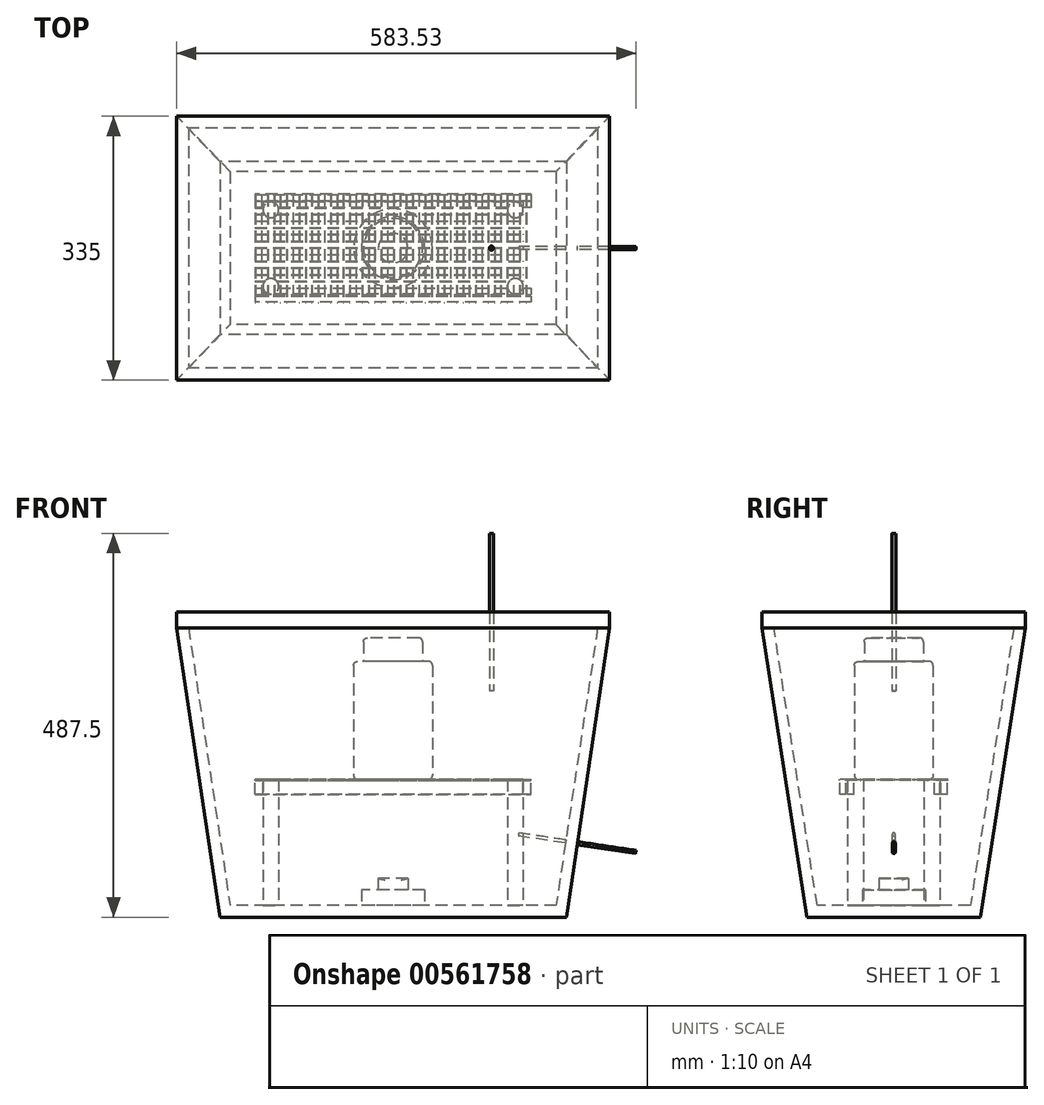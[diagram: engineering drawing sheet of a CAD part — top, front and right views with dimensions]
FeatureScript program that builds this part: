
annotation { "Feature Type Name" : "Feature", "Feature Type Description" : "" }
export const myFeature = defineFeature(function(context is Context, id is Id, definition is map)
    precondition{}
    {
        {
            var Q0;
            Q0=qCreatedBy(makeId("Top.planeOp"),FACE);
            cPlane(context, id + "F0", {"entities" : qUnion([Q0]), "cplaneType" : CPlaneType.OFFSET, "offset" : 200 * mm, "width" : 150 * mm, "height" : 150 * mm});
        }
        {
            var Q0;
            Q0=qCreatedBy(makeId("Top.planeOp"),FACE);
            cPlane(context, id + "F1", {"entities" : qUnion([Q0]), "cplaneType" : CPlaneType.OFFSET, "offset" : 167.5 * mm, "oppositeDirection" : true, "width" : 150 * mm, "height" : 150 * mm});
        }
        {
            var Q0;
            Q0=qCreatedBy(id+"F1.planeOp",FACE);
            var sketch = newSketch(context, id + "F2", { "sketchPlane" : qUnion([Q0])});
            skLineSegment(sketch, "E0.bottom", {"start": v(220, 110) * mm, "end": v(-220, 110) * mm});
            skLineSegment(sketch, "E0.top", {"start": v(220, -110) * mm, "end": v(-220, -110) * mm});
            skLineSegment(sketch, "E0.left", {"start": v(220, 110) * mm, "end": v(220, -110) * mm});
            skLineSegment(sketch, "E0.right", {"start": v(-220, 110) * mm, "end": v(-220, -110) * mm});
            skPoint(sketch, "E0.middle", {"position": v(0, 0) * mm});
            skSolve(sketch);
        }
        {
            var Q0;
            Q0=qCreatedBy(id+"F0.planeOp",FACE);
            var sketch = newSketch(context, id + "F3", { "sketchPlane" : qUnion([Q0])});
            skLineSegment(sketch, "E1.bottom", {"start": v(275, 167.5) * mm, "end": v(-275, 167.5) * mm});
            skLineSegment(sketch, "E1.top", {"start": v(275, -167.5) * mm, "end": v(-275, -167.5) * mm});
            skLineSegment(sketch, "E1.left", {"start": v(275, 167.5) * mm, "end": v(275, -167.5) * mm});
            skLineSegment(sketch, "E1.right", {"start": v(-275, 167.5) * mm, "end": v(-275, -167.5) * mm});
            skPoint(sketch, "E1.middle", {"position": v(0, 0) * mm});
            skSolve(sketch);
        }
        {
            var Q0;
            Q0=makeQuery(id+"F2.imprint","IMPRINT",FACE,{"disambiguationData":[TD([[makeQuery(id+"F2.imprint","IMPRINT",EDGE,{"derivedFrom":sQuery(id+"F2.wireOp",EDGE,"E0.bottom")}),1.0]])]});
            var Q1;
            Q1=makeQuery(id+"F3.imprint","IMPRINT",FACE,{"disambiguationData":[TD([[makeQuery(id+"F3.imprint","IMPRINT",EDGE,{"derivedFrom":sQuery(id+"F3.wireOp",EDGE,"E1.bottom")}),1.0]])]});
            loft(context, id + "F4", {"sheetProfilesArray" : [{ "sheetProfileEntities" : qUnion([Q0]) }, { "sheetProfileEntities" : qUnion([Q1]) }]});
        }
        {
            var Q0;
            Q0=makeQuery(id+"F4.opLoft","CAP_FACE",FACE,{"disambiguationData":[OSD([makeQuery(id+"F3.imprint","IMPRINT",FACE,{"disambiguationData":[TD([[makeQuery(id+"F3.imprint","IMPRINT",EDGE,{"derivedFrom":sQuery(id+"F3.wireOp",EDGE,"E1.bottom")}),1.0]])]})])],"isStart":true});
            shell(context, id + "F5", {"entities" : qUnion([Q0]), "thickness" : 15 * mm});
        }
        {
            var Q0;
            Q0=makeQuery(id+"F5.opShell","OFFSET_FACE",FACE,{"disambiguationData":[OSD([makeQuery(id+"F2.imprint","IMPRINT",FACE,{"disambiguationData":[TD([[makeQuery(id+"F2.imprint","IMPRINT",EDGE,{"derivedFrom":sQuery(id+"F2.wireOp",EDGE,"E0.bottom")}),1.0]])]})])]});
            var sketch = newSketch(context, id + "F6", { "sketchPlane" : qUnion([Q0])});
            skCircle(sketch, "E2", {"center": v(-155.28, 48.56) * mm, "radius": 10 * mm});
            skCircle(sketch, "E3", {"center": v(-155.28, -48.56) * mm, "radius": 10 * mm});
            skCircle(sketch, "E4", {"center": v(155.28, -48.56) * mm, "radius": 10 * mm});
            skCircle(sketch, "E5", {"center": v(155.28, 48.56) * mm, "radius": 10 * mm});
            skSolve(sketch);
        }
        {
            var Q0;
            Q0=makeQuery(id+"F6.imprint","IMPRINT",FACE,{"disambiguationData":[TD([[makeQuery(id+"F6.imprint","IMPRINT",EDGE,{"derivedFrom":sQuery(id+"F6.wireOp",EDGE,"E2")}),1.0]])]});
            var Q1;
            Q1=makeQuery(id+"F6.imprint","IMPRINT",FACE,{"disambiguationData":[TD([[makeQuery(id+"F6.imprint","IMPRINT",EDGE,{"derivedFrom":sQuery(id+"F6.wireOp",EDGE,"E3")}),1.0]])]});
            var Q2;
            Q2=makeQuery(id+"F6.imprint","IMPRINT",FACE,{"disambiguationData":[TD([[makeQuery(id+"F6.imprint","IMPRINT",EDGE,{"derivedFrom":sQuery(id+"F6.wireOp",EDGE,"E5")}),1.0]])]});
            var Q3;
            Q3=makeQuery(id+"F6.imprint","IMPRINT",FACE,{"disambiguationData":[TD([[makeQuery(id+"F6.imprint","IMPRINT",EDGE,{"derivedFrom":sQuery(id+"F6.wireOp",EDGE,"E4")}),1.0]])]});
            extrude(context, id + "F7", {"entities" : qUnion([Q0, Q1, Q2, Q3]), "operationType" : NewBodyOperationType.ADD, "depth" : 160 * mm, "offsetDistance" : 25 * mm});
        }
        {
            var Q0;
            Q0=makeQuery(id+"F7.opExtrude","CAP_FACE",FACE,{"disambiguationData":[OSD([sQuery(id+"F6.wireOp",EDGE,"E2")])],"isStart":false});
            var sketch = newSketch(context, id + "F8", { "sketchPlane" : qUnion([Q0])});
            skLineSegment(sketch, "E6.bottom", {"start": v(-155.28, 48.56) * mm, "end": v(155.28, 48.56) * mm});
            skLineSegment(sketch, "E6.top", {"start": v(-155.28, -48.56) * mm, "end": v(155.28, -48.56) * mm});
            skLineSegment(sketch, "E6.left", {"start": v(-155.28, 48.56) * mm, "end": v(-155.28, -48.56) * mm});
            skLineSegment(sketch, "E6.right", {"start": v(155.28, 48.56) * mm, "end": v(155.28, -48.56) * mm});
            skPoint(sketch, "E6.middle", {"position": v(0, 0) * mm});
            skLineSegment(sketch, "E7.bottom", {"start": v(165.28, 58.56) * mm, "end": v(-165.28, 58.56) * mm});
            skLineSegment(sketch, "E7.top", {"start": v(165.28, -58.56) * mm, "end": v(-165.28, -58.56) * mm});
            skLineSegment(sketch, "E7.left", {"start": v(165.28, 58.56) * mm, "end": v(165.28, -58.56) * mm});
            skLineSegment(sketch, "E7.right", {"start": v(-165.28, 58.56) * mm, "end": v(-165.28, -58.56) * mm});
            skLineSegment(sketch, "E8.bottom", {"start": v(175.28, 68.56) * mm, "end": v(-175.28, 68.56) * mm});
            skLineSegment(sketch, "E8.top", {"start": v(175.28, -68.56) * mm, "end": v(-175.28, -68.56) * mm});
            skLineSegment(sketch, "E8.left", {"start": v(175.28, 68.56) * mm, "end": v(175.28, -68.56) * mm});
            skLineSegment(sketch, "E8.right", {"start": v(-175.28, 68.56) * mm, "end": v(-175.28, -68.56) * mm});
            skLineSegment(sketch, "E9.bottom", {"start": v(-175.28, 68.06) * mm, "end": v(175.28, 68.06) * mm});
            skLineSegment(sketch, "E9.top", {"start": v(-175.28, 60.06) * mm, "end": v(175.28, 60.06) * mm});
            skLineSegment(sketch, "E9.left", {"start": v(-175.28, 68.06) * mm, "end": v(-175.28, 60.06) * mm});
            skLineSegment(sketch, "E9.right", {"start": v(175.28, 68.06) * mm, "end": v(175.28, 60.06) * mm});
            skLineSegment(sketch, "E10.bottom", {"start": v(175.28, 59.56) * mm, "end": v(-175.28, 59.56) * mm});
            skLineSegment(sketch, "E10.top", {"start": v(175.28, 51.56) * mm, "end": v(-175.28, 51.56) * mm});
            skLineSegment(sketch, "E10.left", {"start": v(175.28, 59.56) * mm, "end": v(175.28, 51.56) * mm});
            skLineSegment(sketch, "E10.right", {"start": v(-175.28, 59.56) * mm, "end": v(-175.28, 51.56) * mm});
            skLineSegment(sketch, "E11.bottom", {"start": v(-175.28, 43.06) * mm, "end": v(175.28, 43.06) * mm});
            skLineSegment(sketch, "E11.top", {"start": v(-175.28, 51.06) * mm, "end": v(175.28, 51.06) * mm});
            skLineSegment(sketch, "E11.left", {"start": v(-175.28, 43.06) * mm, "end": v(-175.28, 51.06) * mm});
            skLineSegment(sketch, "E11.right", {"start": v(175.28, 43.06) * mm, "end": v(175.28, 51.06) * mm});
            skLineSegment(sketch, "E12.bottom", {"start": v(-175.28, 42.56) * mm, "end": v(175.28, 42.56) * mm});
            skLineSegment(sketch, "E12.top", {"start": v(-175.28, 34.56) * mm, "end": v(175.28, 34.56) * mm});
            skLineSegment(sketch, "E12.left", {"start": v(-175.28, 42.56) * mm, "end": v(-175.28, 34.56) * mm});
            skLineSegment(sketch, "E12.right", {"start": v(175.28, 42.56) * mm, "end": v(175.28, 34.56) * mm});
            skLineSegment(sketch, "E13.bottom", {"start": v(-175.28, 34.06) * mm, "end": v(175.28, 34.06) * mm});
            skLineSegment(sketch, "E13.top", {"start": v(-175.28, 26.06) * mm, "end": v(175.28, 26.06) * mm});
            skLineSegment(sketch, "E13.left", {"start": v(-175.28, 34.06) * mm, "end": v(-175.28, 26.06) * mm});
            skLineSegment(sketch, "E13.right", {"start": v(175.28, 34.06) * mm, "end": v(175.28, 26.06) * mm});
            skLineSegment(sketch, "E14.bottom", {"start": v(-175.28, 25.56) * mm, "end": v(175.28, 25.56) * mm});
            skLineSegment(sketch, "E14.top", {"start": v(-175.28, 17.56) * mm, "end": v(175.28, 17.56) * mm});
            skLineSegment(sketch, "E14.left", {"start": v(-175.28, 25.56) * mm, "end": v(-175.28, 17.56) * mm});
            skLineSegment(sketch, "E14.right", {"start": v(175.28, 25.56) * mm, "end": v(175.28, 17.56) * mm});
            skLineSegment(sketch, "E15.bottom", {"start": v(-175.28, 17.06) * mm, "end": v(175.28, 17.06) * mm});
            skLineSegment(sketch, "E15.top", {"start": v(-175.28, 9.06) * mm, "end": v(175.28, 9.06) * mm});
            skLineSegment(sketch, "E15.left", {"start": v(-175.28, 17.06) * mm, "end": v(-175.28, 9.06) * mm});
            skLineSegment(sketch, "E15.right", {"start": v(175.28, 17.06) * mm, "end": v(175.28, 9.06) * mm});
            skLineSegment(sketch, "E16.bottom", {"start": v(-175.28, 0.56) * mm, "end": v(175.28, 0.56) * mm});
            skLineSegment(sketch, "E16.top", {"start": v(-175.28, 8.56) * mm, "end": v(175.28, 8.56) * mm});
            skLineSegment(sketch, "E16.left", {"start": v(-175.28, 0.56) * mm, "end": v(-175.28, 8.56) * mm});
            skLineSegment(sketch, "E16.right", {"start": v(175.28, 0.56) * mm, "end": v(175.28, 8.56) * mm});
            skLineSegment(sketch, "E17.bottom", {"start": v(-175.28, -7.94) * mm, "end": v(175.28, -7.94) * mm});
            skLineSegment(sketch, "E17.top", {"start": v(-175.28, 0.06) * mm, "end": v(175.28, 0.06) * mm});
            skLineSegment(sketch, "E17.left", {"start": v(-175.28, -7.94) * mm, "end": v(-175.28, 0.06) * mm});
            skLineSegment(sketch, "E17.right", {"start": v(175.28, -7.94) * mm, "end": v(175.28, 0.06) * mm});
            skLineSegment(sketch, "E18.bottom", {"start": v(-175.28, -8.44) * mm, "end": v(175.28, -8.44) * mm});
            skLineSegment(sketch, "E18.top", {"start": v(-175.28, -16.44) * mm, "end": v(175.28, -16.44) * mm});
            skLineSegment(sketch, "E18.left", {"start": v(-175.28, -8.44) * mm, "end": v(-175.28, -16.44) * mm});
            skLineSegment(sketch, "E18.right", {"start": v(175.28, -8.44) * mm, "end": v(175.28, -16.44) * mm});
            skLineSegment(sketch, "E19.bottom", {"start": v(-175.28, -16.94) * mm, "end": v(175.28, -16.94) * mm});
            skLineSegment(sketch, "E19.top", {"start": v(-175.28, -24.94) * mm, "end": v(175.28, -24.94) * mm});
            skLineSegment(sketch, "E19.left", {"start": v(-175.28, -16.94) * mm, "end": v(-175.28, -24.94) * mm});
            skLineSegment(sketch, "E19.right", {"start": v(175.28, -16.94) * mm, "end": v(175.28, -24.94) * mm});
            skLineSegment(sketch, "E20.bottom", {"start": v(-175.28, -25.44) * mm, "end": v(175.28, -25.44) * mm});
            skLineSegment(sketch, "E20.top", {"start": v(-175.28, -33.44) * mm, "end": v(175.28, -33.44) * mm});
            skLineSegment(sketch, "E20.left", {"start": v(-175.28, -25.44) * mm, "end": v(-175.28, -33.44) * mm});
            skLineSegment(sketch, "E20.right", {"start": v(175.28, -25.44) * mm, "end": v(175.28, -33.44) * mm});
            skLineSegment(sketch, "E21.bottom", {"start": v(-175.28, -33.94) * mm, "end": v(175.28, -33.94) * mm});
            skLineSegment(sketch, "E21.top", {"start": v(-175.28, -41.94) * mm, "end": v(175.28, -41.94) * mm});
            skLineSegment(sketch, "E21.left", {"start": v(-175.28, -33.94) * mm, "end": v(-175.28, -41.94) * mm});
            skLineSegment(sketch, "E21.right", {"start": v(175.28, -33.94) * mm, "end": v(175.28, -41.94) * mm});
            skLineSegment(sketch, "E22.bottom", {"start": v(-175.28, -42.44) * mm, "end": v(175.28, -42.44) * mm});
            skLineSegment(sketch, "E22.top", {"start": v(-175.28, -50.44) * mm, "end": v(175.28, -50.44) * mm});
            skLineSegment(sketch, "E22.left", {"start": v(-175.28, -42.44) * mm, "end": v(-175.28, -50.44) * mm});
            skLineSegment(sketch, "E22.right", {"start": v(175.28, -42.44) * mm, "end": v(175.28, -50.44) * mm});
            skLineSegment(sketch, "E23.bottom", {"start": v(-175.28, -50.94) * mm, "end": v(175.28, -50.94) * mm});
            skLineSegment(sketch, "E23.top", {"start": v(-175.28, -58.94) * mm, "end": v(175.28, -58.94) * mm});
            skLineSegment(sketch, "E23.left", {"start": v(-175.28, -50.94) * mm, "end": v(-175.28, -58.94) * mm});
            skLineSegment(sketch, "E23.right", {"start": v(175.28, -50.94) * mm, "end": v(175.28, -58.94) * mm});
            skLineSegment(sketch, "E24.bottom", {"start": v(-175.28, -60.56) * mm, "end": v(175.28, -60.56) * mm});
            skLineSegment(sketch, "E24.top", {"start": v(-175.28, -68.56) * mm, "end": v(175.28, -68.56) * mm});
            skLineSegment(sketch, "E24.left", {"start": v(-175.28, -60.56) * mm, "end": v(-175.28, -68.56) * mm});
            skLineSegment(sketch, "E24.right", {"start": v(175.28, -60.56) * mm, "end": v(175.28, -68.56) * mm});
            skSolve(sketch);
        }
        {
            var Q0;
            {var subQ5=sQuery(id+"F8.wireOp",EDGE,"E7.top");Q0=makeQuery(id+"F8.imprint","IMPRINT",FACE,{"disambiguationData":[TD([[makeQuery(id+"F8.imprint","IMPRINT",EDGE,{"derivedFrom":subQ5}),1.0]])]});}
            var Q1;
            {var subQ0=sQuery(id+"F8.wireOp",EDGE,"E16.bottom");var subQ1=sQuery(id+"F8.wireOp",EDGE,"E7.right");var subQ2=makeQuery(id+"F8.imprint","INTERSECT",VERTEX,{"derivedFrom":[subQ1,subQ0]});Q1=makeQuery(id+"F8.imprint","IMPRINT",FACE,{"disambiguationData":[TD([[makeQuery(id+"F8.imprint","IMPRINT",EDGE,{"disambiguationData":[TD([[subQ2,-1.0]])],"derivedFrom":subQ1}),-1.0]])]});}
            var Q2;
            {var subQ0=sQuery(id+"F8.wireOp",EDGE,"E13.top");var subQ1=sQuery(id+"F8.wireOp",EDGE,"E7.right");var subQ2=makeQuery(id+"F8.imprint","INTERSECT",VERTEX,{"derivedFrom":[subQ1,subQ0]});Q2=makeQuery(id+"F8.imprint","IMPRINT",FACE,{"disambiguationData":[TD([[makeQuery(id+"F8.imprint","IMPRINT",EDGE,{"disambiguationData":[TD([[subQ2,-1.0]])],"derivedFrom":subQ1}),-1.0]])]});}
            var Q3;
            {var subQ0=sQuery(id+"F8.wireOp",EDGE,"E13.top");var subQ1=sQuery(id+"F8.wireOp",EDGE,"E6.right");var subQ2=makeQuery(id+"F8.imprint","INTERSECT",VERTEX,{"derivedFrom":[subQ1,subQ0]});Q3=makeQuery(id+"F8.imprint","IMPRINT",FACE,{"disambiguationData":[TD([[makeQuery(id+"F8.imprint","IMPRINT",EDGE,{"disambiguationData":[TD([[subQ2,-1.0]])],"derivedFrom":subQ1}),1.0]])]});}
            var Q4;
            {var subQ0=sQuery(id+"F8.wireOp",EDGE,"E13.top");var subQ1=sQuery(id+"F8.wireOp",EDGE,"E6.left");var subQ2=makeQuery(id+"F8.imprint","INTERSECT",VERTEX,{"derivedFrom":[subQ1,subQ0]});Q4=makeQuery(id+"F8.imprint","IMPRINT",FACE,{"disambiguationData":[TD([[makeQuery(id+"F8.imprint","IMPRINT",EDGE,{"disambiguationData":[TD([[subQ2,-1.0]])],"derivedFrom":subQ1}),-1.0]])]});}
            var Q5;
            {var subQ0=sQuery(id+"F8.wireOp",EDGE,"E20.top");var subQ1=sQuery(id+"F8.wireOp",EDGE,"E6.left");var subQ2=makeQuery(id+"F8.imprint","INTERSECT",VERTEX,{"derivedFrom":[subQ1,subQ0]});Q5=makeQuery(id+"F8.imprint","IMPRINT",FACE,{"disambiguationData":[TD([[makeQuery(id+"F8.imprint","IMPRINT",EDGE,{"disambiguationData":[TD([[subQ2,-1.0]])],"derivedFrom":subQ1}),-1.0]])]});}
            var Q6;
            {var subQ0=sQuery(id+"F8.wireOp",EDGE,"E16.bottom");var subQ1=sQuery(id+"F8.wireOp",EDGE,"E6.left");var subQ2=makeQuery(id+"F8.imprint","INTERSECT",VERTEX,{"derivedFrom":[subQ1,subQ0]});Q6=makeQuery(id+"F8.imprint","IMPRINT",FACE,{"disambiguationData":[TD([[makeQuery(id+"F8.imprint","IMPRINT",EDGE,{"disambiguationData":[TD([[subQ2,-1.0]])],"derivedFrom":subQ1}),-1.0]])]});}
            var Q7;
            {var subQ0=sQuery(id+"F8.wireOp",EDGE,"E15.top");var subQ1=sQuery(id+"F8.wireOp",EDGE,"E6.left");var subQ2=makeQuery(id+"F8.imprint","INTERSECT",VERTEX,{"derivedFrom":[subQ1,subQ0]});Q7=makeQuery(id+"F8.imprint","IMPRINT",FACE,{"disambiguationData":[TD([[makeQuery(id+"F8.imprint","IMPRINT",EDGE,{"disambiguationData":[TD([[subQ2,-1.0]])],"derivedFrom":subQ1}),1.0]])]});}
            var Q8;
            {var subQ0=sQuery(id+"F8.wireOp",EDGE,"E19.top");var subQ1=sQuery(id+"F8.wireOp",EDGE,"E6.left");var subQ2=makeQuery(id+"F8.imprint","INTERSECT",VERTEX,{"derivedFrom":[subQ1,subQ0]});Q8=makeQuery(id+"F8.imprint","IMPRINT",FACE,{"disambiguationData":[TD([[makeQuery(id+"F8.imprint","IMPRINT",EDGE,{"disambiguationData":[TD([[subQ2,-1.0]])],"derivedFrom":subQ1}),1.0]])]});}
            var Q9;
            {var subQ0=sQuery(id+"F8.wireOp",EDGE,"E12.top");var subQ1=sQuery(id+"F8.wireOp",EDGE,"E6.left");var subQ2=makeQuery(id+"F8.imprint","INTERSECT",VERTEX,{"derivedFrom":[subQ1,subQ0]});Q9=makeQuery(id+"F8.imprint","IMPRINT",FACE,{"disambiguationData":[TD([[makeQuery(id+"F8.imprint","IMPRINT",EDGE,{"disambiguationData":[TD([[subQ2,-1.0]])],"derivedFrom":subQ1}),-1.0]])]});}
            var Q10;
            {var subQ0=sQuery(id+"F8.wireOp",EDGE,"E10.top");var subQ1=sQuery(id+"F8.wireOp",EDGE,"E7.left");var subQ2=makeQuery(id+"F8.imprint","INTERSECT",VERTEX,{"derivedFrom":[subQ1,subQ0]});Q10=makeQuery(id+"F8.imprint","IMPRINT",FACE,{"disambiguationData":[TD([[makeQuery(id+"F8.imprint","IMPRINT",EDGE,{"disambiguationData":[TD([[subQ2,-1.0]])],"derivedFrom":subQ1}),-1.0]])]});}
            var Q11;
            {var subQ0=sQuery(id+"F8.wireOp",EDGE,"E16.bottom");var subQ1=sQuery(id+"F8.wireOp",EDGE,"E6.right");var subQ2=makeQuery(id+"F8.imprint","INTERSECT",VERTEX,{"derivedFrom":[subQ1,subQ0]});Q11=makeQuery(id+"F8.imprint","IMPRINT",FACE,{"disambiguationData":[TD([[makeQuery(id+"F8.imprint","IMPRINT",EDGE,{"disambiguationData":[TD([[subQ2,-1.0]])],"derivedFrom":subQ1}),1.0]])]});}
            var Q12;
            {var subQ0=sQuery(id+"F8.wireOp",EDGE,"E18.top");var subQ1=sQuery(id+"F8.wireOp",EDGE,"E6.left");var subQ2=makeQuery(id+"F8.imprint","INTERSECT",VERTEX,{"derivedFrom":[subQ1,subQ0]});Q12=makeQuery(id+"F8.imprint","IMPRINT",FACE,{"disambiguationData":[TD([[makeQuery(id+"F8.imprint","IMPRINT",EDGE,{"disambiguationData":[TD([[subQ2,-1.0]])],"derivedFrom":subQ1}),-1.0]])]});}
            var Q13;
            {var subQ0=sQuery(id+"F8.wireOp",EDGE,"E17.bottom");var subQ1=sQuery(id+"F8.wireOp",EDGE,"E6.right");var subQ2=makeQuery(id+"F8.imprint","INTERSECT",VERTEX,{"derivedFrom":[subQ1,subQ0]});Q13=makeQuery(id+"F8.imprint","IMPRINT",FACE,{"disambiguationData":[TD([[makeQuery(id+"F8.imprint","IMPRINT",EDGE,{"disambiguationData":[TD([[subQ2,-1.0]])],"derivedFrom":subQ1}),1.0]])]});}
            var Q14;
            {var subQ0=sQuery(id+"F8.wireOp",EDGE,"E21.top");var subQ1=sQuery(id+"F8.wireOp",EDGE,"E7.right");var subQ2=makeQuery(id+"F8.imprint","INTERSECT",VERTEX,{"derivedFrom":[subQ1,subQ0]});Q14=makeQuery(id+"F8.imprint","IMPRINT",FACE,{"disambiguationData":[TD([[makeQuery(id+"F8.imprint","IMPRINT",EDGE,{"disambiguationData":[TD([[subQ2,-1.0]])],"derivedFrom":subQ1}),-1.0]])]});}
            var Q15;
            {var subQ0=sQuery(id+"F8.wireOp",EDGE,"E19.top");var subQ1=sQuery(id+"F8.wireOp",EDGE,"E6.right");var subQ2=makeQuery(id+"F8.imprint","INTERSECT",VERTEX,{"derivedFrom":[subQ1,subQ0]});Q15=makeQuery(id+"F8.imprint","IMPRINT",FACE,{"disambiguationData":[TD([[makeQuery(id+"F8.imprint","IMPRINT",EDGE,{"disambiguationData":[TD([[subQ2,-1.0]])],"derivedFrom":subQ1}),1.0]])]});}
            var Q16;
            {var subQ0=sQuery(id+"F8.wireOp",EDGE,"E17.bottom");var subQ1=sQuery(id+"F8.wireOp",EDGE,"E6.left");var subQ2=makeQuery(id+"F8.imprint","INTERSECT",VERTEX,{"derivedFrom":[subQ1,subQ0]});Q16=makeQuery(id+"F8.imprint","IMPRINT",FACE,{"disambiguationData":[TD([[makeQuery(id+"F8.imprint","IMPRINT",EDGE,{"disambiguationData":[TD([[subQ2,-1.0]])],"derivedFrom":subQ1}),-1.0]])]});}
            var Q17;
            {var subQ0=sQuery(id+"F8.wireOp",EDGE,"E21.top");var subQ1=sQuery(id+"F8.wireOp",EDGE,"E6.left");var subQ2=makeQuery(id+"F8.imprint","INTERSECT",VERTEX,{"derivedFrom":[subQ1,subQ0]});Q17=makeQuery(id+"F8.imprint","IMPRINT",FACE,{"disambiguationData":[TD([[makeQuery(id+"F8.imprint","IMPRINT",EDGE,{"disambiguationData":[TD([[subQ2,-1.0]])],"derivedFrom":subQ1}),1.0]])]});}
            var Q18;
            {var subQ0=sQuery(id+"F8.wireOp",EDGE,"E15.top");var subQ1=sQuery(id+"F8.wireOp",EDGE,"E7.right");var subQ2=makeQuery(id+"F8.imprint","INTERSECT",VERTEX,{"derivedFrom":[subQ1,subQ0]});Q18=makeQuery(id+"F8.imprint","IMPRINT",FACE,{"disambiguationData":[TD([[makeQuery(id+"F8.imprint","IMPRINT",EDGE,{"disambiguationData":[TD([[subQ2,-1.0]])],"derivedFrom":subQ1}),-1.0]])]});}
            var Q19;
            {var subQ0=sQuery(id+"F8.wireOp",EDGE,"E16.bottom");var subQ1=sQuery(id+"F8.wireOp",EDGE,"E6.left");var subQ2=makeQuery(id+"F8.imprint","INTERSECT",VERTEX,{"derivedFrom":[subQ1,subQ0]});Q19=makeQuery(id+"F8.imprint","IMPRINT",FACE,{"disambiguationData":[TD([[makeQuery(id+"F8.imprint","IMPRINT",EDGE,{"disambiguationData":[TD([[subQ2,-1.0]])],"derivedFrom":subQ1}),1.0]])]});}
            var Q20;
            {var subQ0=sQuery(id+"F8.wireOp",EDGE,"E18.top");var subQ1=sQuery(id+"F8.wireOp",EDGE,"E6.right");var subQ2=makeQuery(id+"F8.imprint","INTERSECT",VERTEX,{"derivedFrom":[subQ1,subQ0]});Q20=makeQuery(id+"F8.imprint","IMPRINT",FACE,{"disambiguationData":[TD([[makeQuery(id+"F8.imprint","IMPRINT",EDGE,{"disambiguationData":[TD([[subQ2,-1.0]])],"derivedFrom":subQ1}),1.0]])]});}
            var Q21;
            {var subQ0=sQuery(id+"F8.wireOp",EDGE,"E15.top");var subQ1=sQuery(id+"F8.wireOp",EDGE,"E6.right");var subQ2=makeQuery(id+"F8.imprint","INTERSECT",VERTEX,{"derivedFrom":[subQ1,subQ0]});Q21=makeQuery(id+"F8.imprint","IMPRINT",FACE,{"disambiguationData":[TD([[makeQuery(id+"F8.imprint","IMPRINT",EDGE,{"disambiguationData":[TD([[subQ2,-1.0]])],"derivedFrom":subQ1}),1.0]])]});}
            var Q22;
            {var subQ0=sQuery(id+"F8.wireOp",EDGE,"E20.top");var subQ1=sQuery(id+"F8.wireOp",EDGE,"E6.left");var subQ2=makeQuery(id+"F8.imprint","INTERSECT",VERTEX,{"derivedFrom":[subQ1,subQ0]});Q22=makeQuery(id+"F8.imprint","IMPRINT",FACE,{"disambiguationData":[TD([[makeQuery(id+"F8.imprint","IMPRINT",EDGE,{"disambiguationData":[TD([[subQ2,-1.0]])],"derivedFrom":subQ1}),1.0]])]});}
            var Q23;
            {var subQ0=sQuery(id+"F8.wireOp",EDGE,"E17.bottom");var subQ1=sQuery(id+"F8.wireOp",EDGE,"E7.right");var subQ2=makeQuery(id+"F8.imprint","INTERSECT",VERTEX,{"derivedFrom":[subQ1,subQ0]});Q23=makeQuery(id+"F8.imprint","IMPRINT",FACE,{"disambiguationData":[TD([[makeQuery(id+"F8.imprint","IMPRINT",EDGE,{"disambiguationData":[TD([[subQ2,-1.0]])],"derivedFrom":subQ1}),-1.0]])]});}
            var Q24;
            {var subQ0=sQuery(id+"F8.wireOp",EDGE,"E14.top");var subQ1=sQuery(id+"F8.wireOp",EDGE,"E6.left");var subQ2=makeQuery(id+"F8.imprint","INTERSECT",VERTEX,{"derivedFrom":[subQ1,subQ0]});Q24=makeQuery(id+"F8.imprint","IMPRINT",FACE,{"disambiguationData":[TD([[makeQuery(id+"F8.imprint","IMPRINT",EDGE,{"disambiguationData":[TD([[subQ2,-1.0]])],"derivedFrom":subQ1}),-1.0]])]});}
            var Q25;
            {var subQ0=sQuery(id+"F8.wireOp",EDGE,"E12.top");var subQ1=sQuery(id+"F8.wireOp",EDGE,"E6.left");var subQ2=makeQuery(id+"F8.imprint","INTERSECT",VERTEX,{"derivedFrom":[subQ1,subQ0]});Q25=makeQuery(id+"F8.imprint","IMPRINT",FACE,{"disambiguationData":[TD([[makeQuery(id+"F8.imprint","IMPRINT",EDGE,{"disambiguationData":[TD([[subQ2,-1.0]])],"derivedFrom":subQ1}),1.0]])]});}
            var Q26;
            {var subQ0=sQuery(id+"F8.wireOp",EDGE,"E18.top");var subQ1=sQuery(id+"F8.wireOp",EDGE,"E7.right");var subQ2=makeQuery(id+"F8.imprint","INTERSECT",VERTEX,{"derivedFrom":[subQ1,subQ0]});Q26=makeQuery(id+"F8.imprint","IMPRINT",FACE,{"disambiguationData":[TD([[makeQuery(id+"F8.imprint","IMPRINT",EDGE,{"disambiguationData":[TD([[subQ2,-1.0]])],"derivedFrom":subQ1}),-1.0]])]});}
            var Q27;
            {var subQ0=sQuery(id+"F8.wireOp",EDGE,"E20.top");var subQ1=sQuery(id+"F8.wireOp",EDGE,"E6.right");var subQ2=makeQuery(id+"F8.imprint","INTERSECT",VERTEX,{"derivedFrom":[subQ1,subQ0]});Q27=makeQuery(id+"F8.imprint","IMPRINT",FACE,{"disambiguationData":[TD([[makeQuery(id+"F8.imprint","IMPRINT",EDGE,{"disambiguationData":[TD([[subQ2,-1.0]])],"derivedFrom":subQ1}),1.0]])]});}
            var Q28;
            {var subQ0=sQuery(id+"F8.wireOp",EDGE,"E12.top");var subQ1=sQuery(id+"F8.wireOp",EDGE,"E6.right");var subQ2=makeQuery(id+"F8.imprint","INTERSECT",VERTEX,{"derivedFrom":[subQ1,subQ0]});Q28=makeQuery(id+"F8.imprint","IMPRINT",FACE,{"disambiguationData":[TD([[makeQuery(id+"F8.imprint","IMPRINT",EDGE,{"disambiguationData":[TD([[subQ2,-1.0]])],"derivedFrom":subQ1}),1.0]])]});}
            var Q29;
            Q29=makeQuery(id+"F7.opExtrude","CAP_FACE",FACE,{"disambiguationData":[OSD([sQuery(id+"F6.wireOp",EDGE,"E4")])],"isStart":false});
            var Q30;
            Q30=makeQuery(id+"F7.opExtrude","CAP_FACE",FACE,{"disambiguationData":[OSD([sQuery(id+"F6.wireOp",EDGE,"E3")])],"isStart":false});
            var Q31;
            Q31=makeQuery(id+"F7.opExtrude","CAP_FACE",FACE,{"disambiguationData":[OSD([sQuery(id+"F6.wireOp",EDGE,"E2")])],"isStart":false});
            var Q32;
            Q32=makeQuery(id+"F7.opExtrude","CAP_FACE",FACE,{"disambiguationData":[OSD([sQuery(id+"F6.wireOp",EDGE,"E5")])],"isStart":false});
            var Q33;
            {var subQ0=sQuery(id+"F8.wireOp",EDGE,"E6.left");var subQ1=sQuery(id+"F8.wireOp",EDGE,"E6.bottom");var subQ2=makeQuery(id+"F8.imprint","INTERSECT",VERTEX,{"derivedFrom":[subQ1,subQ0]});Q33=makeQuery(id+"F8.imprint","IMPRINT",FACE,{"disambiguationData":[TD([[makeQuery(id+"F8.imprint","IMPRINT",EDGE,{"disambiguationData":[TD([[subQ2,-1.0]])],"derivedFrom":subQ1}),-1.0]])]});}
            var Q34;
            {var subQ0=sQuery(id+"F8.wireOp",EDGE,"E7.top");Q34=makeQuery(id+"F8.imprint","IMPRINT",FACE,{"disambiguationData":[TD([[makeQuery(id+"F8.imprint","IMPRINT",EDGE,{"derivedFrom":subQ0}),-1.0]])]});}
            var Q35;
            {var subQ0=sQuery(id+"F8.wireOp",EDGE,"E11.bottom");var subQ1=sQuery(id+"F8.wireOp",EDGE,"E6.right");var subQ2=makeQuery(id+"F8.imprint","INTERSECT",VERTEX,{"derivedFrom":[subQ1,subQ0]});Q35=makeQuery(id+"F8.imprint","IMPRINT",FACE,{"disambiguationData":[TD([[makeQuery(id+"F8.imprint","IMPRINT",EDGE,{"disambiguationData":[TD([[subQ2,-1.0]])],"derivedFrom":subQ1}),-1.0]])]});}
            var Q36;
            {var subQ0=sQuery(id+"F8.wireOp",EDGE,"E10.top");var subQ1=makeQuery(id+"F7.opExtrude","CAP_EDGE",EDGE,{"disambiguationData":[OSD([sQuery(id+"F6.wireOp",EDGE,"E2")])],"isStart":false});var subQ2=makeQuery(id+"F8.imprint","INTERSECT",VERTEX,{"disambiguationData":[OD(0.0)],"derivedFrom":[subQ1,subQ0]});Q36=makeQuery(id+"F8.imprint","IMPRINT",FACE,{"disambiguationData":[TD([[makeQuery(id+"F8.imprint","IMPRINT",EDGE,{"disambiguationData":[TD([[subQ2,-1.0]])],"derivedFrom":subQ0}),-1.0]])]});}
            var Q37;
            {var subQ0=sQuery(id+"F8.wireOp",EDGE,"E13.top");var subQ1=sQuery(id+"F8.wireOp",EDGE,"E6.left");var subQ2=makeQuery(id+"F8.imprint","INTERSECT",VERTEX,{"derivedFrom":[subQ1,subQ0]});Q37=makeQuery(id+"F8.imprint","IMPRINT",FACE,{"disambiguationData":[TD([[makeQuery(id+"F8.imprint","IMPRINT",EDGE,{"disambiguationData":[TD([[subQ2,-1.0]])],"derivedFrom":subQ1}),1.0]])]});}
            var Q38;
            {var subQ0=sQuery(id+"F8.wireOp",EDGE,"E17.bottom");var subQ1=sQuery(id+"F8.wireOp",EDGE,"E6.left");var subQ2=makeQuery(id+"F8.imprint","INTERSECT",VERTEX,{"derivedFrom":[subQ1,subQ0]});Q38=makeQuery(id+"F8.imprint","IMPRINT",FACE,{"disambiguationData":[TD([[makeQuery(id+"F8.imprint","IMPRINT",EDGE,{"disambiguationData":[TD([[subQ2,-1.0]])],"derivedFrom":subQ1}),1.0]])]});}
            var Q39;
            {var subQ0=sQuery(id+"F8.wireOp",EDGE,"E11.bottom");var subQ1=sQuery(id+"F8.wireOp",EDGE,"E6.right");var subQ2=makeQuery(id+"F8.imprint","INTERSECT",VERTEX,{"derivedFrom":[subQ1,subQ0]});Q39=makeQuery(id+"F8.imprint","IMPRINT",FACE,{"disambiguationData":[TD([[makeQuery(id+"F8.imprint","IMPRINT",EDGE,{"disambiguationData":[TD([[subQ2,-1.0]])],"derivedFrom":subQ1}),1.0]])]});}
            var Q40;
            {var subQ0=sQuery(id+"F8.wireOp",EDGE,"E14.top");var subQ1=sQuery(id+"F8.wireOp",EDGE,"E6.right");var subQ2=makeQuery(id+"F8.imprint","INTERSECT",VERTEX,{"derivedFrom":[subQ1,subQ0]});Q40=makeQuery(id+"F8.imprint","IMPRINT",FACE,{"disambiguationData":[TD([[makeQuery(id+"F8.imprint","IMPRINT",EDGE,{"disambiguationData":[TD([[subQ2,-1.0]])],"derivedFrom":subQ1}),1.0]])]});}
            var Q41;
            {var subQ0=sQuery(id+"F8.wireOp",EDGE,"E22.top");var subQ1=sQuery(id+"F8.wireOp",EDGE,"E7.right");var subQ2=makeQuery(id+"F8.imprint","INTERSECT",VERTEX,{"derivedFrom":[subQ1,subQ0]});Q41=makeQuery(id+"F8.imprint","IMPRINT",FACE,{"disambiguationData":[TD([[makeQuery(id+"F8.imprint","IMPRINT",EDGE,{"disambiguationData":[TD([[subQ2,-1.0]])],"derivedFrom":subQ1}),-1.0]])]});}
            var Q42;
            {var subQ0=sQuery(id+"F8.wireOp",EDGE,"E14.top");var subQ1=sQuery(id+"F8.wireOp",EDGE,"E7.right");var subQ2=makeQuery(id+"F8.imprint","INTERSECT",VERTEX,{"derivedFrom":[subQ1,subQ0]});Q42=makeQuery(id+"F8.imprint","IMPRINT",FACE,{"disambiguationData":[TD([[makeQuery(id+"F8.imprint","IMPRINT",EDGE,{"disambiguationData":[TD([[subQ2,-1.0]])],"derivedFrom":subQ1}),-1.0]])]});}
            var Q43;
            {var subQ0=sQuery(id+"F8.wireOp",EDGE,"E10.top");var subQ1=sQuery(id+"F8.wireOp",EDGE,"E7.right");var subQ2=makeQuery(id+"F8.imprint","INTERSECT",VERTEX,{"derivedFrom":[subQ1,subQ0]});Q43=makeQuery(id+"F8.imprint","IMPRINT",FACE,{"disambiguationData":[TD([[makeQuery(id+"F8.imprint","IMPRINT",EDGE,{"disambiguationData":[TD([[subQ2,-1.0]])],"derivedFrom":subQ1}),-1.0]])]});}
            var Q44;
            {var subQ0=sQuery(id+"F8.wireOp",EDGE,"E19.top");var subQ1=sQuery(id+"F8.wireOp",EDGE,"E6.left");var subQ2=makeQuery(id+"F8.imprint","INTERSECT",VERTEX,{"derivedFrom":[subQ1,subQ0]});Q44=makeQuery(id+"F8.imprint","IMPRINT",FACE,{"disambiguationData":[TD([[makeQuery(id+"F8.imprint","IMPRINT",EDGE,{"disambiguationData":[TD([[subQ2,-1.0]])],"derivedFrom":subQ1}),-1.0]])]});}
            var Q45;
            {var subQ0=sQuery(id+"F8.wireOp",EDGE,"E15.top");var subQ1=sQuery(id+"F8.wireOp",EDGE,"E6.left");var subQ2=makeQuery(id+"F8.imprint","INTERSECT",VERTEX,{"derivedFrom":[subQ1,subQ0]});Q45=makeQuery(id+"F8.imprint","IMPRINT",FACE,{"disambiguationData":[TD([[makeQuery(id+"F8.imprint","IMPRINT",EDGE,{"disambiguationData":[TD([[subQ2,-1.0]])],"derivedFrom":subQ1}),-1.0]])]});}
            var Q46;
            {var subQ0=sQuery(id+"F8.wireOp",EDGE,"E21.top");var subQ1=sQuery(id+"F8.wireOp",EDGE,"E6.right");var subQ2=makeQuery(id+"F8.imprint","INTERSECT",VERTEX,{"derivedFrom":[subQ1,subQ0]});Q46=makeQuery(id+"F8.imprint","IMPRINT",FACE,{"disambiguationData":[TD([[makeQuery(id+"F8.imprint","IMPRINT",EDGE,{"disambiguationData":[TD([[subQ2,-1.0]])],"derivedFrom":subQ1}),1.0]])]});}
            var Q47;
            {var subQ0=sQuery(id+"F8.wireOp",EDGE,"E12.top");var subQ1=sQuery(id+"F8.wireOp",EDGE,"E7.right");var subQ2=makeQuery(id+"F8.imprint","INTERSECT",VERTEX,{"derivedFrom":[subQ1,subQ0]});Q47=makeQuery(id+"F8.imprint","IMPRINT",FACE,{"disambiguationData":[TD([[makeQuery(id+"F8.imprint","IMPRINT",EDGE,{"disambiguationData":[TD([[subQ2,-1.0]])],"derivedFrom":subQ1}),-1.0]])]});}
            var Q48;
            {var subQ0=sQuery(id+"F8.wireOp",EDGE,"E20.top");var subQ1=sQuery(id+"F8.wireOp",EDGE,"E7.right");var subQ2=makeQuery(id+"F8.imprint","INTERSECT",VERTEX,{"derivedFrom":[subQ1,subQ0]});Q48=makeQuery(id+"F8.imprint","IMPRINT",FACE,{"disambiguationData":[TD([[makeQuery(id+"F8.imprint","IMPRINT",EDGE,{"disambiguationData":[TD([[subQ2,-1.0]])],"derivedFrom":subQ1}),-1.0]])]});}
            var Q49;
            {var subQ0=sQuery(id+"F8.wireOp",EDGE,"E11.bottom");var subQ1=sQuery(id+"F8.wireOp",EDGE,"E6.left");var subQ2=makeQuery(id+"F8.imprint","INTERSECT",VERTEX,{"derivedFrom":[subQ1,subQ0]});Q49=makeQuery(id+"F8.imprint","IMPRINT",FACE,{"disambiguationData":[TD([[makeQuery(id+"F8.imprint","IMPRINT",EDGE,{"disambiguationData":[TD([[subQ2,-1.0]])],"derivedFrom":subQ1}),-1.0]])]});}
            var Q50;
            Q50=makeQuery(id+"F6.imprint","IMPRINT",FACE,{"disambiguationData":[TD([[makeQuery(id+"F6.imprint","IMPRINT",EDGE,{"derivedFrom":sQuery(id+"F6.wireOp",EDGE,"E3")}),1.0]])]});
            var Q51;
            {var subQ0=sQuery(id+"F8.wireOp",EDGE,"E19.top");var subQ1=sQuery(id+"F8.wireOp",EDGE,"E7.right");var subQ2=makeQuery(id+"F8.imprint","INTERSECT",VERTEX,{"derivedFrom":[subQ1,subQ0]});Q51=makeQuery(id+"F8.imprint","IMPRINT",FACE,{"disambiguationData":[TD([[makeQuery(id+"F8.imprint","IMPRINT",EDGE,{"disambiguationData":[TD([[subQ2,-1.0]])],"derivedFrom":subQ1}),-1.0]])]});}
            var Q52;
            Q52=makeQuery(id+"F6.imprint","IMPRINT",FACE,{"disambiguationData":[TD([[makeQuery(id+"F6.imprint","IMPRINT",EDGE,{"derivedFrom":sQuery(id+"F6.wireOp",EDGE,"E4")}),1.0]])]});
            var Q53;
            {var subQ0=sQuery(id+"F8.wireOp",EDGE,"E11.bottom");var subQ1=sQuery(id+"F8.wireOp",EDGE,"E7.right");var subQ2=makeQuery(id+"F8.imprint","INTERSECT",VERTEX,{"derivedFrom":[subQ1,subQ0]});Q53=makeQuery(id+"F8.imprint","IMPRINT",FACE,{"disambiguationData":[TD([[makeQuery(id+"F8.imprint","IMPRINT",EDGE,{"disambiguationData":[TD([[subQ2,-1.0]])],"derivedFrom":subQ1}),-1.0]])]});}
            var Q54;
            {var subQ0=sQuery(id+"F8.wireOp",EDGE,"E18.top");var subQ1=sQuery(id+"F8.wireOp",EDGE,"E6.left");var subQ2=makeQuery(id+"F8.imprint","INTERSECT",VERTEX,{"derivedFrom":[subQ1,subQ0]});Q54=makeQuery(id+"F8.imprint","IMPRINT",FACE,{"disambiguationData":[TD([[makeQuery(id+"F8.imprint","IMPRINT",EDGE,{"disambiguationData":[TD([[subQ2,-1.0]])],"derivedFrom":subQ1}),1.0]])]});}
            var Q55;
            {var subQ0=sQuery(id+"F8.wireOp",EDGE,"E14.top");var subQ1=sQuery(id+"F8.wireOp",EDGE,"E6.left");var subQ2=makeQuery(id+"F8.imprint","INTERSECT",VERTEX,{"derivedFrom":[subQ1,subQ0]});Q55=makeQuery(id+"F8.imprint","IMPRINT",FACE,{"disambiguationData":[TD([[makeQuery(id+"F8.imprint","IMPRINT",EDGE,{"disambiguationData":[TD([[subQ2,-1.0]])],"derivedFrom":subQ1}),1.0]])]});}
            var Q56;
            {var subQ0=sQuery(id+"F8.wireOp",EDGE,"E12.bottom");var subQ1=sQuery(id+"F8.wireOp",EDGE,"E6.left");var subQ2=makeQuery(id+"F8.imprint","INTERSECT",VERTEX,{"derivedFrom":[subQ1,subQ0]});Q56=makeQuery(id+"F8.imprint","IMPRINT",FACE,{"disambiguationData":[TD([[makeQuery(id+"F8.imprint","IMPRINT",EDGE,{"disambiguationData":[TD([[subQ2,-1.0]])],"derivedFrom":subQ1}),1.0]])]});}
            var Q57;
            {var subQ0=sQuery(id+"F8.wireOp",EDGE,"E21.top");var subQ1=sQuery(id+"F8.wireOp",EDGE,"E6.left");var subQ2=makeQuery(id+"F8.imprint","INTERSECT",VERTEX,{"derivedFrom":[subQ1,subQ0]});Q57=makeQuery(id+"F8.imprint","IMPRINT",FACE,{"disambiguationData":[TD([[makeQuery(id+"F8.imprint","IMPRINT",EDGE,{"disambiguationData":[TD([[subQ2,-1.0]])],"derivedFrom":subQ1}),-1.0]])]});}
            var Q58;
            {var subQ5=sQuery(id+"F8.wireOp",EDGE,"E6.left");var subQ8=sQuery(id+"F8.wireOp",EDGE,"E6.bottom");var subQ9=makeQuery(id+"F8.imprint","INTERSECT",VERTEX,{"derivedFrom":[subQ8,subQ5]});Q58=makeQuery(id+"F8.imprint","IMPRINT",FACE,{"disambiguationData":[TD([[makeQuery(id+"F8.imprint","IMPRINT",EDGE,{"disambiguationData":[TD([[subQ9,-1.0]])],"derivedFrom":subQ8}),1.0]])]});}
            var Q59;
            {var subQ0=sQuery(id+"F8.wireOp",EDGE,"E11.bottom");var subQ1=sQuery(id+"F8.wireOp",EDGE,"E6.left");var subQ2=makeQuery(id+"F8.imprint","INTERSECT",VERTEX,{"derivedFrom":[subQ1,subQ0]});Q59=makeQuery(id+"F8.imprint","IMPRINT",FACE,{"disambiguationData":[TD([[makeQuery(id+"F8.imprint","IMPRINT",EDGE,{"disambiguationData":[TD([[subQ2,-1.0]])],"derivedFrom":subQ1}),1.0]])]});}
            var Q60;
            {var subQ0=sQuery(id+"F8.wireOp",EDGE,"E22.top");var subQ1=sQuery(id+"F8.wireOp",EDGE,"E7.left");var subQ2=makeQuery(id+"F8.imprint","INTERSECT",VERTEX,{"derivedFrom":[subQ1,subQ0]});Q60=makeQuery(id+"F8.imprint","IMPRINT",FACE,{"disambiguationData":[TD([[makeQuery(id+"F8.imprint","IMPRINT",EDGE,{"disambiguationData":[TD([[subQ2,-1.0]])],"derivedFrom":subQ1}),-1.0]])]});}
            var Q61;
            {var subQ0=sQuery(id+"F8.wireOp",EDGE,"E12.bottom");var subQ1=sQuery(id+"F8.wireOp",EDGE,"E6.left");var subQ2=makeQuery(id+"F8.imprint","INTERSECT",VERTEX,{"derivedFrom":[subQ1,subQ0]});Q61=makeQuery(id+"F8.imprint","IMPRINT",FACE,{"disambiguationData":[TD([[makeQuery(id+"F8.imprint","IMPRINT",EDGE,{"disambiguationData":[TD([[subQ2,-1.0]])],"derivedFrom":subQ1}),-1.0]])]});}
            var Q62;
            Q62=makeQuery(id+"F6.imprint","IMPRINT",FACE,{"disambiguationData":[TD([[makeQuery(id+"F6.imprint","IMPRINT",EDGE,{"derivedFrom":sQuery(id+"F6.wireOp",EDGE,"E5")}),1.0]])]});
            var Q63;
            {var subQ0=sQuery(id+"F8.wireOp",EDGE,"E10.top");var subQ1=makeQuery(id+"F7.opExtrude","CAP_EDGE",EDGE,{"disambiguationData":[OSD([sQuery(id+"F6.wireOp",EDGE,"E2")])],"isStart":false});var subQ2=makeQuery(id+"F8.imprint","INTERSECT",VERTEX,{"disambiguationData":[OD(0.0)],"derivedFrom":[subQ1,subQ0]});Q63=makeQuery(id+"F8.imprint","IMPRINT",FACE,{"disambiguationData":[TD([[makeQuery(id+"F8.imprint","IMPRINT",EDGE,{"disambiguationData":[TD([[subQ2,-1.0]])],"derivedFrom":subQ0}),1.0]])]});}
            var Q64;
            {var subQ0=sQuery(id+"F8.wireOp",EDGE,"E11.bottom");var subQ1=sQuery(id+"F8.wireOp",EDGE,"E7.right");var subQ2=makeQuery(id+"F8.imprint","INTERSECT",VERTEX,{"derivedFrom":[subQ1,subQ0]});Q64=makeQuery(id+"F8.imprint","IMPRINT",FACE,{"disambiguationData":[TD([[makeQuery(id+"F8.imprint","IMPRINT",EDGE,{"disambiguationData":[TD([[subQ2,-1.0]])],"derivedFrom":subQ1}),1.0]])]});}
            var Q65;
            Q65=makeQuery(id+"F6.imprint","IMPRINT",FACE,{"disambiguationData":[TD([[makeQuery(id+"F6.imprint","IMPRINT",EDGE,{"derivedFrom":sQuery(id+"F6.wireOp",EDGE,"E2")}),1.0]])]});
            var Q66;
            {var subQ0=sQuery(id+"F8.wireOp",EDGE,"E10.top");var subQ1=sQuery(id+"F8.wireOp",EDGE,"E7.right");var subQ2=makeQuery(id+"F8.imprint","INTERSECT",VERTEX,{"derivedFrom":[subQ1,subQ0]});Q66=makeQuery(id+"F8.imprint","IMPRINT",FACE,{"disambiguationData":[TD([[makeQuery(id+"F8.imprint","IMPRINT",EDGE,{"disambiguationData":[TD([[subQ2,-1.0]])],"derivedFrom":subQ1}),1.0]])]});}
            var Q67;
            {var subQ0=sQuery(id+"F8.wireOp",EDGE,"E8.bottom");Q67=makeQuery(id+"F8.imprint","IMPRINT",FACE,{"disambiguationData":[TD([[makeQuery(id+"F8.imprint","IMPRINT",EDGE,{"derivedFrom":subQ0}),1.0]])]});}
            var Q68;
            {var subQ0=sQuery(id+"F8.wireOp",EDGE,"E9.top");Q68=makeQuery(id+"F8.imprint","IMPRINT",FACE,{"disambiguationData":[TD([[makeQuery(id+"F8.imprint","IMPRINT",EDGE,{"derivedFrom":subQ0}),-1.0]])]});}
            extrude(context, id + "F9", {"entities" : qUnion([Q0, Q1, Q2, Q3, Q4, Q5, Q6, Q7, Q8, Q9, Q10, Q11, Q12, Q13, Q14, Q15, Q16, Q17, Q18, Q19, Q20, Q21, Q22, Q23, Q24, Q25, Q26, Q27, Q28, Q29, Q30, Q31, Q32, Q33, Q34, Q35, Q36, Q37, Q38, Q39, Q40, Q41, Q42, Q43, Q44, Q45, Q46, Q47, Q48, Q49, Q50, Q51, Q52, Q53, Q54, Q55, Q56, Q57, Q58, Q59, Q60, Q61, Q62, Q63, Q64, Q65, Q66, Q67, Q68]), "operationType" : NewBodyOperationType.ADD, "oppositeDirection" : true, "depth" : 1 * mm, "offsetDistance" : 25 * mm});
        }
        {
            var Q0;
            Q0=makeQuery(id+"F8.imprint","IMPRINT",FACE,{"disambiguationData":[TD([[makeQuery(id+"F8.imprint","IMPRINT",EDGE,{"derivedFrom":sQuery(id+"F8.wireOp",EDGE,"E24.bottom")}),-1.0]])]});
            var Q1;
            {var subQ5=sQuery(id+"F8.wireOp",EDGE,"E23.right");Q1=makeQuery(id+"F8.imprint","IMPRINT",FACE,{"disambiguationData":[TD([[makeQuery(id+"F8.imprint","IMPRINT",EDGE,{"derivedFrom":subQ5}),-1.0]])]});}
            var Q2;
            {var subQ5=sQuery(id+"F8.wireOp",EDGE,"E22.right");Q2=makeQuery(id+"F8.imprint","IMPRINT",FACE,{"disambiguationData":[TD([[makeQuery(id+"F8.imprint","IMPRINT",EDGE,{"derivedFrom":subQ5}),-1.0]])]});}
            var Q3;
            {var subQ5=sQuery(id+"F8.wireOp",EDGE,"E21.right");Q3=makeQuery(id+"F8.imprint","IMPRINT",FACE,{"disambiguationData":[TD([[makeQuery(id+"F8.imprint","IMPRINT",EDGE,{"derivedFrom":subQ5}),-1.0]])]});}
            var Q4;
            {var subQ5=sQuery(id+"F8.wireOp",EDGE,"E20.right");Q4=makeQuery(id+"F8.imprint","IMPRINT",FACE,{"disambiguationData":[TD([[makeQuery(id+"F8.imprint","IMPRINT",EDGE,{"derivedFrom":subQ5}),-1.0]])]});}
            var Q5;
            {var subQ5=sQuery(id+"F8.wireOp",EDGE,"E19.right");Q5=makeQuery(id+"F8.imprint","IMPRINT",FACE,{"disambiguationData":[TD([[makeQuery(id+"F8.imprint","IMPRINT",EDGE,{"derivedFrom":subQ5}),-1.0]])]});}
            var Q6;
            {var subQ5=sQuery(id+"F8.wireOp",EDGE,"E18.right");Q6=makeQuery(id+"F8.imprint","IMPRINT",FACE,{"disambiguationData":[TD([[makeQuery(id+"F8.imprint","IMPRINT",EDGE,{"derivedFrom":subQ5}),-1.0]])]});}
            var Q7;
            {var subQ5=sQuery(id+"F8.wireOp",EDGE,"E17.right");Q7=makeQuery(id+"F8.imprint","IMPRINT",FACE,{"disambiguationData":[TD([[makeQuery(id+"F8.imprint","IMPRINT",EDGE,{"derivedFrom":subQ5}),1.0]])]});}
            var Q8;
            {var subQ5=sQuery(id+"F8.wireOp",EDGE,"E16.right");Q8=makeQuery(id+"F8.imprint","IMPRINT",FACE,{"disambiguationData":[TD([[makeQuery(id+"F8.imprint","IMPRINT",EDGE,{"derivedFrom":subQ5}),1.0]])]});}
            var Q9;
            {var subQ5=sQuery(id+"F8.wireOp",EDGE,"E15.right");Q9=makeQuery(id+"F8.imprint","IMPRINT",FACE,{"disambiguationData":[TD([[makeQuery(id+"F8.imprint","IMPRINT",EDGE,{"derivedFrom":subQ5}),-1.0]])]});}
            var Q10;
            {var subQ5=sQuery(id+"F8.wireOp",EDGE,"E14.right");Q10=makeQuery(id+"F8.imprint","IMPRINT",FACE,{"disambiguationData":[TD([[makeQuery(id+"F8.imprint","IMPRINT",EDGE,{"derivedFrom":subQ5}),-1.0]])]});}
            var Q11;
            {var subQ5=sQuery(id+"F8.wireOp",EDGE,"E13.right");Q11=makeQuery(id+"F8.imprint","IMPRINT",FACE,{"disambiguationData":[TD([[makeQuery(id+"F8.imprint","IMPRINT",EDGE,{"derivedFrom":subQ5}),-1.0]])]});}
            var Q12;
            {var subQ5=sQuery(id+"F8.wireOp",EDGE,"E12.right");Q12=makeQuery(id+"F8.imprint","IMPRINT",FACE,{"disambiguationData":[TD([[makeQuery(id+"F8.imprint","IMPRINT",EDGE,{"derivedFrom":subQ5}),-1.0]])]});}
            var Q13;
            {var subQ5=sQuery(id+"F8.wireOp",EDGE,"E11.right");Q13=makeQuery(id+"F8.imprint","IMPRINT",FACE,{"disambiguationData":[TD([[makeQuery(id+"F8.imprint","IMPRINT",EDGE,{"derivedFrom":subQ5}),1.0]])]});}
            var Q14;
            Q14=makeQuery(id+"F8.imprint","IMPRINT",FACE,{"disambiguationData":[TD([[makeQuery(id+"F8.imprint","IMPRINT",EDGE,{"derivedFrom":sQuery(id+"F8.wireOp",EDGE,"E10.bottom")}),1.0]])]});
            var Q15;
            Q15=makeQuery(id+"F8.imprint","IMPRINT",FACE,{"disambiguationData":[TD([[makeQuery(id+"F8.imprint","IMPRINT",EDGE,{"derivedFrom":sQuery(id+"F8.wireOp",EDGE,"E9.bottom")}),-1.0]])]});
            var Q16;
            {var subQ0=sQuery(id+"F8.wireOp",EDGE,"E11.left");Q16=makeQuery(id+"F8.imprint","IMPRINT",FACE,{"disambiguationData":[TD([[makeQuery(id+"F8.imprint","IMPRINT",EDGE,{"derivedFrom":subQ0}),-1.0]])]});}
            var Q17;
            {var subQ5=sQuery(id+"F8.wireOp",EDGE,"E12.left");Q17=makeQuery(id+"F8.imprint","IMPRINT",FACE,{"disambiguationData":[TD([[makeQuery(id+"F8.imprint","IMPRINT",EDGE,{"derivedFrom":subQ5}),1.0]])]});}
            var Q18;
            {var subQ5=sQuery(id+"F8.wireOp",EDGE,"E13.left");Q18=makeQuery(id+"F8.imprint","IMPRINT",FACE,{"disambiguationData":[TD([[makeQuery(id+"F8.imprint","IMPRINT",EDGE,{"derivedFrom":subQ5}),1.0]])]});}
            var Q19;
            {var subQ5=sQuery(id+"F8.wireOp",EDGE,"E14.left");Q19=makeQuery(id+"F8.imprint","IMPRINT",FACE,{"disambiguationData":[TD([[makeQuery(id+"F8.imprint","IMPRINT",EDGE,{"derivedFrom":subQ5}),1.0]])]});}
            var Q20;
            {var subQ5=sQuery(id+"F8.wireOp",EDGE,"E15.left");Q20=makeQuery(id+"F8.imprint","IMPRINT",FACE,{"disambiguationData":[TD([[makeQuery(id+"F8.imprint","IMPRINT",EDGE,{"derivedFrom":subQ5}),1.0]])]});}
            var Q21;
            {var subQ5=sQuery(id+"F8.wireOp",EDGE,"E16.left");Q21=makeQuery(id+"F8.imprint","IMPRINT",FACE,{"disambiguationData":[TD([[makeQuery(id+"F8.imprint","IMPRINT",EDGE,{"derivedFrom":subQ5}),-1.0]])]});}
            var Q22;
            {var subQ5=sQuery(id+"F8.wireOp",EDGE,"E17.left");Q22=makeQuery(id+"F8.imprint","IMPRINT",FACE,{"disambiguationData":[TD([[makeQuery(id+"F8.imprint","IMPRINT",EDGE,{"derivedFrom":subQ5}),-1.0]])]});}
            var Q23;
            {var subQ5=sQuery(id+"F8.wireOp",EDGE,"E18.left");Q23=makeQuery(id+"F8.imprint","IMPRINT",FACE,{"disambiguationData":[TD([[makeQuery(id+"F8.imprint","IMPRINT",EDGE,{"derivedFrom":subQ5}),1.0]])]});}
            var Q24;
            {var subQ5=sQuery(id+"F8.wireOp",EDGE,"E19.left");Q24=makeQuery(id+"F8.imprint","IMPRINT",FACE,{"disambiguationData":[TD([[makeQuery(id+"F8.imprint","IMPRINT",EDGE,{"derivedFrom":subQ5}),1.0]])]});}
            var Q25;
            {var subQ5=sQuery(id+"F8.wireOp",EDGE,"E20.left");Q25=makeQuery(id+"F8.imprint","IMPRINT",FACE,{"disambiguationData":[TD([[makeQuery(id+"F8.imprint","IMPRINT",EDGE,{"derivedFrom":subQ5}),1.0]])]});}
            var Q26;
            {var subQ5=sQuery(id+"F8.wireOp",EDGE,"E21.left");Q26=makeQuery(id+"F8.imprint","IMPRINT",FACE,{"disambiguationData":[TD([[makeQuery(id+"F8.imprint","IMPRINT",EDGE,{"derivedFrom":subQ5}),1.0]])]});}
            var Q27;
            {var subQ5=sQuery(id+"F8.wireOp",EDGE,"E22.left");Q27=makeQuery(id+"F8.imprint","IMPRINT",FACE,{"disambiguationData":[TD([[makeQuery(id+"F8.imprint","IMPRINT",EDGE,{"derivedFrom":subQ5}),1.0]])]});}
            var Q28;
            {var subQ5=sQuery(id+"F8.wireOp",EDGE,"E23.left");Q28=makeQuery(id+"F8.imprint","IMPRINT",FACE,{"disambiguationData":[TD([[makeQuery(id+"F8.imprint","IMPRINT",EDGE,{"derivedFrom":subQ5}),1.0]])]});}
            var Q29;
            {var subQ5=sQuery(id+"F8.wireOp",EDGE,"E7.top");Q29=makeQuery(id+"F8.imprint","IMPRINT",FACE,{"disambiguationData":[TD([[makeQuery(id+"F8.imprint","IMPRINT",EDGE,{"derivedFrom":subQ5}),1.0]])]});}
            extrude(context, id + "F10", {"entities" : qUnion([Q0, Q1, Q2, Q3, Q4, Q5, Q6, Q7, Q8, Q9, Q10, Q11, Q12, Q13, Q14, Q15, Q16, Q17, Q18, Q19, Q20, Q21, Q22, Q23, Q24, Q25, Q26, Q27, Q28, Q29]), "oppositeDirection" : true, "depth" : 19.05 * mm, "offsetDistance" : 25 * mm});
        }
        {
            var Q0;
            Q0=makeQuery(id+"F10.opExtrude","CAP_FACE",FACE,{"disambiguationData":[OSD([sQuery(id+"F8.wireOp",EDGE,"E9.bottom"),sQuery(id+"F8.wireOp",EDGE,"E9.top"),sQuery(id+"F8.wireOp",EDGE,"E9.left"),sQuery(id+"F8.wireOp",EDGE,"E9.right")])],"isStart":true});
            var sketch = newSketch(context, id + "F11", { "sketchPlane" : qUnion([Q0])});
            skLineSegment(sketch, "E25.bottom", {"start": v(-175.28, 68.06) * mm, "end": v(-174.78, 68.06) * mm});
            skLineSegment(sketch, "E25.top", {"start": v(-175.28, -68.95) * mm, "end": v(-174.78, -68.95) * mm});
            skLineSegment(sketch, "E25.left", {"start": v(-175.28, 68.06) * mm, "end": v(-175.28, -68.95) * mm});
            skLineSegment(sketch, "E25.right", {"start": v(-174.78, 68.06) * mm, "end": v(-174.78, -68.95) * mm});
            skLineSegment(sketch, "E26.1.0.0", {"start": v(-166.78, 68.06) * mm, "end": v(-166.78, -68.95) * mm});
            skLineSegment(sketch, "E26.1.0.1", {"start": v(-167.28, 68.06) * mm, "end": v(-167.28, -68.95) * mm});
            skLineSegment(sketch, "E26.1.0.2", {"start": v(-167.28, 68.06) * mm, "end": v(-166.78, 68.06) * mm});
            skLineSegment(sketch, "E26.1.0.3", {"start": v(-167.28, -68.95) * mm, "end": v(-166.78, -68.95) * mm});
            skLineSegment(sketch, "E26.direction1", {"start": v(-174.78, -68.95) * mm, "end": v(-166.78, -68.95) * mm, "construction": true});
            skLineSegment(sketch, "E27.0.2.0", {"start": v(-158.78, 68.06) * mm, "end": v(-158.78, -68.95) * mm});
            skLineSegment(sketch, "E27.3.2.0", {"start": v(-159.28, 68.06) * mm, "end": v(-159.28, -68.95) * mm});
            skLineSegment(sketch, "E27.6.2.0", {"start": v(-159.28, 68.06) * mm, "end": v(-158.78, 68.06) * mm});
            skLineSegment(sketch, "E27.9.2.0", {"start": v(-159.28, -68.95) * mm, "end": v(-158.78, -68.95) * mm});
            skLineSegment(sketch, "E28.0.3.0", {"start": v(-150.78, 68.06) * mm, "end": v(-150.78, -68.95) * mm});
            skLineSegment(sketch, "E28.3.3.0", {"start": v(-151.28, 68.06) * mm, "end": v(-151.28, -68.95) * mm});
            skLineSegment(sketch, "E28.6.3.0", {"start": v(-151.28, 68.06) * mm, "end": v(-150.78, 68.06) * mm});
            skLineSegment(sketch, "E28.9.3.0", {"start": v(-151.28, -68.95) * mm, "end": v(-150.78, -68.95) * mm});
            skLineSegment(sketch, "E28.0.4.0", {"start": v(-142.78, 68.06) * mm, "end": v(-142.78, -68.95) * mm});
            skLineSegment(sketch, "E28.3.4.0", {"start": v(-143.28, 68.06) * mm, "end": v(-143.28, -68.95) * mm});
            skLineSegment(sketch, "E28.6.4.0", {"start": v(-143.28, 68.06) * mm, "end": v(-142.78, 68.06) * mm});
            skLineSegment(sketch, "E28.9.4.0", {"start": v(-143.28, -68.95) * mm, "end": v(-142.78, -68.95) * mm});
            skLineSegment(sketch, "E28.0.5.0", {"start": v(-134.78, 68.06) * mm, "end": v(-134.78, -68.95) * mm});
            skLineSegment(sketch, "E28.3.5.0", {"start": v(-135.28, 68.06) * mm, "end": v(-135.28, -68.95) * mm});
            skLineSegment(sketch, "E28.6.5.0", {"start": v(-135.28, 68.06) * mm, "end": v(-134.78, 68.06) * mm});
            skLineSegment(sketch, "E28.9.5.0", {"start": v(-135.28, -68.95) * mm, "end": v(-134.78, -68.95) * mm});
            skLineSegment(sketch, "E28.0.6.0", {"start": v(-126.78, 68.06) * mm, "end": v(-126.78, -68.95) * mm});
            skLineSegment(sketch, "E28.3.6.0", {"start": v(-127.28, 68.06) * mm, "end": v(-127.28, -68.95) * mm});
            skLineSegment(sketch, "E28.6.6.0", {"start": v(-127.28, 68.06) * mm, "end": v(-126.78, 68.06) * mm});
            skLineSegment(sketch, "E28.9.6.0", {"start": v(-127.28, -68.95) * mm, "end": v(-126.78, -68.95) * mm});
            skLineSegment(sketch, "E28.0.7.0", {"start": v(-118.78, 68.06) * mm, "end": v(-118.78, -68.95) * mm});
            skLineSegment(sketch, "E28.3.7.0", {"start": v(-119.28, 68.06) * mm, "end": v(-119.28, -68.95) * mm});
            skLineSegment(sketch, "E28.6.7.0", {"start": v(-119.28, 68.06) * mm, "end": v(-118.78, 68.06) * mm});
            skLineSegment(sketch, "E28.9.7.0", {"start": v(-119.28, -68.95) * mm, "end": v(-118.78, -68.95) * mm});
            skLineSegment(sketch, "E28.0.8.0", {"start": v(-110.78, 68.06) * mm, "end": v(-110.78, -68.95) * mm});
            skLineSegment(sketch, "E28.3.8.0", {"start": v(-111.28, 68.06) * mm, "end": v(-111.28, -68.95) * mm});
            skLineSegment(sketch, "E28.6.8.0", {"start": v(-111.28, 68.06) * mm, "end": v(-110.78, 68.06) * mm});
            skLineSegment(sketch, "E28.9.8.0", {"start": v(-111.28, -68.95) * mm, "end": v(-110.78, -68.95) * mm});
            skLineSegment(sketch, "E28.0.9.0", {"start": v(-102.78, 68.06) * mm, "end": v(-102.78, -68.95) * mm});
            skLineSegment(sketch, "E28.3.9.0", {"start": v(-103.28, 68.06) * mm, "end": v(-103.28, -68.95) * mm});
            skLineSegment(sketch, "E28.6.9.0", {"start": v(-103.28, 68.06) * mm, "end": v(-102.78, 68.06) * mm});
            skLineSegment(sketch, "E28.9.9.0", {"start": v(-103.28, -68.95) * mm, "end": v(-102.78, -68.95) * mm});
            skLineSegment(sketch, "E29.0.10.0", {"start": v(-94.78, 68.06) * mm, "end": v(-94.78, -68.95) * mm});
            skLineSegment(sketch, "E29.3.10.0", {"start": v(-95.28, 68.06) * mm, "end": v(-95.28, -68.95) * mm});
            skLineSegment(sketch, "E29.6.10.0", {"start": v(-95.28, 68.06) * mm, "end": v(-94.78, 68.06) * mm});
            skLineSegment(sketch, "E29.9.10.0", {"start": v(-95.28, -68.95) * mm, "end": v(-94.78, -68.95) * mm});
            skLineSegment(sketch, "E29.0.11.0", {"start": v(-86.78, 68.06) * mm, "end": v(-86.78, -68.95) * mm});
            skLineSegment(sketch, "E29.3.11.0", {"start": v(-87.28, 68.06) * mm, "end": v(-87.28, -68.95) * mm});
            skLineSegment(sketch, "E29.6.11.0", {"start": v(-87.28, 68.06) * mm, "end": v(-86.78, 68.06) * mm});
            skLineSegment(sketch, "E29.9.11.0", {"start": v(-87.28, -68.95) * mm, "end": v(-86.78, -68.95) * mm});
            skLineSegment(sketch, "E29.0.12.0", {"start": v(-78.78, 68.06) * mm, "end": v(-78.78, -68.95) * mm});
            skLineSegment(sketch, "E29.3.12.0", {"start": v(-79.28, 68.06) * mm, "end": v(-79.28, -68.95) * mm});
            skLineSegment(sketch, "E29.6.12.0", {"start": v(-79.28, 68.06) * mm, "end": v(-78.78, 68.06) * mm});
            skLineSegment(sketch, "E29.9.12.0", {"start": v(-79.28, -68.95) * mm, "end": v(-78.78, -68.95) * mm});
            skLineSegment(sketch, "E29.0.13.0", {"start": v(-70.78, 68.06) * mm, "end": v(-70.78, -68.95) * mm});
            skLineSegment(sketch, "E29.3.13.0", {"start": v(-71.28, 68.06) * mm, "end": v(-71.28, -68.95) * mm});
            skLineSegment(sketch, "E29.6.13.0", {"start": v(-71.28, 68.06) * mm, "end": v(-70.78, 68.06) * mm});
            skLineSegment(sketch, "E29.9.13.0", {"start": v(-71.28, -68.95) * mm, "end": v(-70.78, -68.95) * mm});
            skLineSegment(sketch, "E29.0.14.0", {"start": v(-62.78, 68.06) * mm, "end": v(-62.78, -68.95) * mm});
            skLineSegment(sketch, "E29.3.14.0", {"start": v(-63.28, 68.06) * mm, "end": v(-63.28, -68.95) * mm});
            skLineSegment(sketch, "E29.6.14.0", {"start": v(-63.28, 68.06) * mm, "end": v(-62.78, 68.06) * mm});
            skLineSegment(sketch, "E29.9.14.0", {"start": v(-63.28, -68.95) * mm, "end": v(-62.78, -68.95) * mm});
            skLineSegment(sketch, "E29.0.15.0", {"start": v(-54.78, 68.06) * mm, "end": v(-54.78, -68.95) * mm});
            skLineSegment(sketch, "E29.3.15.0", {"start": v(-55.28, 68.06) * mm, "end": v(-55.28, -68.95) * mm});
            skLineSegment(sketch, "E29.6.15.0", {"start": v(-55.28, 68.06) * mm, "end": v(-54.78, 68.06) * mm});
            skLineSegment(sketch, "E29.9.15.0", {"start": v(-55.28, -68.95) * mm, "end": v(-54.78, -68.95) * mm});
            skLineSegment(sketch, "E29.0.16.0", {"start": v(-46.78, 68.06) * mm, "end": v(-46.78, -68.95) * mm});
            skLineSegment(sketch, "E29.3.16.0", {"start": v(-47.28, 68.06) * mm, "end": v(-47.28, -68.95) * mm});
            skLineSegment(sketch, "E29.6.16.0", {"start": v(-47.28, 68.06) * mm, "end": v(-46.78, 68.06) * mm});
            skLineSegment(sketch, "E29.9.16.0", {"start": v(-47.28, -68.95) * mm, "end": v(-46.78, -68.95) * mm});
            skLineSegment(sketch, "E29.0.17.0", {"start": v(-38.78, 68.06) * mm, "end": v(-38.78, -68.95) * mm});
            skLineSegment(sketch, "E29.3.17.0", {"start": v(-39.28, 68.06) * mm, "end": v(-39.28, -68.95) * mm});
            skLineSegment(sketch, "E29.6.17.0", {"start": v(-39.28, 68.06) * mm, "end": v(-38.78, 68.06) * mm});
            skLineSegment(sketch, "E29.9.17.0", {"start": v(-39.28, -68.95) * mm, "end": v(-38.78, -68.95) * mm});
            skLineSegment(sketch, "E29.0.18.0", {"start": v(-30.78, 68.06) * mm, "end": v(-30.78, -68.95) * mm});
            skLineSegment(sketch, "E29.3.18.0", {"start": v(-31.28, 68.06) * mm, "end": v(-31.28, -68.95) * mm});
            skLineSegment(sketch, "E29.6.18.0", {"start": v(-31.28, 68.06) * mm, "end": v(-30.78, 68.06) * mm});
            skLineSegment(sketch, "E29.9.18.0", {"start": v(-31.28, -68.95) * mm, "end": v(-30.78, -68.95) * mm});
            skLineSegment(sketch, "E29.0.19.0", {"start": v(-22.78, 68.06) * mm, "end": v(-22.78, -68.95) * mm});
            skLineSegment(sketch, "E29.3.19.0", {"start": v(-23.28, 68.06) * mm, "end": v(-23.28, -68.95) * mm});
            skLineSegment(sketch, "E29.6.19.0", {"start": v(-23.28, 68.06) * mm, "end": v(-22.78, 68.06) * mm});
            skLineSegment(sketch, "E29.9.19.0", {"start": v(-23.28, -68.95) * mm, "end": v(-22.78, -68.95) * mm});
            skLineSegment(sketch, "E29.0.20.0", {"start": v(-14.78, 68.06) * mm, "end": v(-14.78, -68.95) * mm});
            skLineSegment(sketch, "E29.3.20.0", {"start": v(-15.28, 68.06) * mm, "end": v(-15.28, -68.95) * mm});
            skLineSegment(sketch, "E29.6.20.0", {"start": v(-15.28, 68.06) * mm, "end": v(-14.78, 68.06) * mm});
            skLineSegment(sketch, "E29.9.20.0", {"start": v(-15.28, -68.95) * mm, "end": v(-14.78, -68.95) * mm});
            skLineSegment(sketch, "E29.0.21.0", {"start": v(-6.78, 68.06) * mm, "end": v(-6.78, -68.95) * mm});
            skLineSegment(sketch, "E29.3.21.0", {"start": v(-7.28, 68.06) * mm, "end": v(-7.28, -68.95) * mm});
            skLineSegment(sketch, "E29.6.21.0", {"start": v(-7.28, 68.06) * mm, "end": v(-6.78, 68.06) * mm});
            skLineSegment(sketch, "E29.9.21.0", {"start": v(-7.28, -68.95) * mm, "end": v(-6.78, -68.95) * mm});
            skLineSegment(sketch, "E29.0.22.0", {"start": v(1.22, 68.06) * mm, "end": v(1.22, -68.95) * mm});
            skLineSegment(sketch, "E29.3.22.0", {"start": v(0.72, 68.06) * mm, "end": v(0.72, -68.95) * mm});
            skLineSegment(sketch, "E29.6.22.0", {"start": v(0.72, 68.06) * mm, "end": v(1.22, 68.06) * mm});
            skLineSegment(sketch, "E29.9.22.0", {"start": v(0.72, -68.95) * mm, "end": v(1.22, -68.95) * mm});
            skLineSegment(sketch, "E29.0.23.0", {"start": v(9.22, 68.06) * mm, "end": v(9.22, -68.95) * mm});
            skLineSegment(sketch, "E29.3.23.0", {"start": v(8.72, 68.06) * mm, "end": v(8.72, -68.95) * mm});
            skLineSegment(sketch, "E29.6.23.0", {"start": v(8.72, 68.06) * mm, "end": v(9.22, 68.06) * mm});
            skLineSegment(sketch, "E29.9.23.0", {"start": v(8.72, -68.95) * mm, "end": v(9.22, -68.95) * mm});
            skLineSegment(sketch, "E29.0.24.0", {"start": v(17.22, 68.06) * mm, "end": v(17.22, -68.95) * mm});
            skLineSegment(sketch, "E29.3.24.0", {"start": v(16.72, 68.06) * mm, "end": v(16.72, -68.95) * mm});
            skLineSegment(sketch, "E29.6.24.0", {"start": v(16.72, 68.06) * mm, "end": v(17.22, 68.06) * mm});
            skLineSegment(sketch, "E29.9.24.0", {"start": v(16.72, -68.95) * mm, "end": v(17.22, -68.95) * mm});
            skLineSegment(sketch, "E29.0.25.0", {"start": v(25.22, 68.06) * mm, "end": v(25.22, -68.95) * mm});
            skLineSegment(sketch, "E29.3.25.0", {"start": v(24.72, 68.06) * mm, "end": v(24.72, -68.95) * mm});
            skLineSegment(sketch, "E29.6.25.0", {"start": v(24.72, 68.06) * mm, "end": v(25.22, 68.06) * mm});
            skLineSegment(sketch, "E29.9.25.0", {"start": v(24.72, -68.95) * mm, "end": v(25.22, -68.95) * mm});
            skLineSegment(sketch, "E29.0.26.0", {"start": v(33.22, 68.06) * mm, "end": v(33.22, -68.95) * mm});
            skLineSegment(sketch, "E29.3.26.0", {"start": v(32.72, 68.06) * mm, "end": v(32.72, -68.95) * mm});
            skLineSegment(sketch, "E29.6.26.0", {"start": v(32.72, 68.06) * mm, "end": v(33.22, 68.06) * mm});
            skLineSegment(sketch, "E29.9.26.0", {"start": v(32.72, -68.95) * mm, "end": v(33.22, -68.95) * mm});
            skLineSegment(sketch, "E29.0.27.0", {"start": v(41.22, 68.06) * mm, "end": v(41.22, -68.95) * mm});
            skLineSegment(sketch, "E29.3.27.0", {"start": v(40.72, 68.06) * mm, "end": v(40.72, -68.95) * mm});
            skLineSegment(sketch, "E29.6.27.0", {"start": v(40.72, 68.06) * mm, "end": v(41.22, 68.06) * mm});
            skLineSegment(sketch, "E29.9.27.0", {"start": v(40.72, -68.95) * mm, "end": v(41.22, -68.95) * mm});
            skLineSegment(sketch, "E29.0.28.0", {"start": v(49.22, 68.06) * mm, "end": v(49.22, -68.95) * mm});
            skLineSegment(sketch, "E29.3.28.0", {"start": v(48.72, 68.06) * mm, "end": v(48.72, -68.95) * mm});
            skLineSegment(sketch, "E29.6.28.0", {"start": v(48.72, 68.06) * mm, "end": v(49.22, 68.06) * mm});
            skLineSegment(sketch, "E29.9.28.0", {"start": v(48.72, -68.95) * mm, "end": v(49.22, -68.95) * mm});
            skLineSegment(sketch, "E29.0.29.0", {"start": v(57.22, 68.06) * mm, "end": v(57.22, -68.95) * mm});
            skLineSegment(sketch, "E29.3.29.0", {"start": v(56.72, 68.06) * mm, "end": v(56.72, -68.95) * mm});
            skLineSegment(sketch, "E29.6.29.0", {"start": v(56.72, 68.06) * mm, "end": v(57.22, 68.06) * mm});
            skLineSegment(sketch, "E29.9.29.0", {"start": v(56.72, -68.95) * mm, "end": v(57.22, -68.95) * mm});
            skLineSegment(sketch, "E29.0.30.0", {"start": v(65.22, 68.06) * mm, "end": v(65.22, -68.95) * mm});
            skLineSegment(sketch, "E29.3.30.0", {"start": v(64.72, 68.06) * mm, "end": v(64.72, -68.95) * mm});
            skLineSegment(sketch, "E29.6.30.0", {"start": v(64.72, 68.06) * mm, "end": v(65.22, 68.06) * mm});
            skLineSegment(sketch, "E29.9.30.0", {"start": v(64.72, -68.95) * mm, "end": v(65.22, -68.95) * mm});
            skLineSegment(sketch, "E29.0.31.0", {"start": v(73.22, 68.06) * mm, "end": v(73.22, -68.95) * mm});
            skLineSegment(sketch, "E29.3.31.0", {"start": v(72.72, 68.06) * mm, "end": v(72.72, -68.95) * mm});
            skLineSegment(sketch, "E29.6.31.0", {"start": v(72.72, 68.06) * mm, "end": v(73.22, 68.06) * mm});
            skLineSegment(sketch, "E29.9.31.0", {"start": v(72.72, -68.95) * mm, "end": v(73.22, -68.95) * mm});
            skLineSegment(sketch, "E29.0.32.0", {"start": v(81.22, 68.06) * mm, "end": v(81.22, -68.95) * mm});
            skLineSegment(sketch, "E29.3.32.0", {"start": v(80.72, 68.06) * mm, "end": v(80.72, -68.95) * mm});
            skLineSegment(sketch, "E29.6.32.0", {"start": v(80.72, 68.06) * mm, "end": v(81.22, 68.06) * mm});
            skLineSegment(sketch, "E29.9.32.0", {"start": v(80.72, -68.95) * mm, "end": v(81.22, -68.95) * mm});
            skLineSegment(sketch, "E29.0.33.0", {"start": v(89.22, 68.06) * mm, "end": v(89.22, -68.95) * mm});
            skLineSegment(sketch, "E29.3.33.0", {"start": v(88.72, 68.06) * mm, "end": v(88.72, -68.95) * mm});
            skLineSegment(sketch, "E29.6.33.0", {"start": v(88.72, 68.06) * mm, "end": v(89.22, 68.06) * mm});
            skLineSegment(sketch, "E29.9.33.0", {"start": v(88.72, -68.95) * mm, "end": v(89.22, -68.95) * mm});
            skLineSegment(sketch, "E29.0.34.0", {"start": v(97.22, 68.06) * mm, "end": v(97.22, -68.95) * mm});
            skLineSegment(sketch, "E29.3.34.0", {"start": v(96.72, 68.06) * mm, "end": v(96.72, -68.95) * mm});
            skLineSegment(sketch, "E29.6.34.0", {"start": v(96.72, 68.06) * mm, "end": v(97.22, 68.06) * mm});
            skLineSegment(sketch, "E29.9.34.0", {"start": v(96.72, -68.95) * mm, "end": v(97.22, -68.95) * mm});
            skLineSegment(sketch, "E29.0.35.0", {"start": v(105.22, 68.06) * mm, "end": v(105.22, -68.95) * mm});
            skLineSegment(sketch, "E29.3.35.0", {"start": v(104.72, 68.06) * mm, "end": v(104.72, -68.95) * mm});
            skLineSegment(sketch, "E29.6.35.0", {"start": v(104.72, 68.06) * mm, "end": v(105.22, 68.06) * mm});
            skLineSegment(sketch, "E29.9.35.0", {"start": v(104.72, -68.95) * mm, "end": v(105.22, -68.95) * mm});
            skLineSegment(sketch, "E29.0.36.0", {"start": v(113.22, 68.06) * mm, "end": v(113.22, -68.95) * mm});
            skLineSegment(sketch, "E29.3.36.0", {"start": v(112.72, 68.06) * mm, "end": v(112.72, -68.95) * mm});
            skLineSegment(sketch, "E29.6.36.0", {"start": v(112.72, 68.06) * mm, "end": v(113.22, 68.06) * mm});
            skLineSegment(sketch, "E29.9.36.0", {"start": v(112.72, -68.95) * mm, "end": v(113.22, -68.95) * mm});
            skLineSegment(sketch, "E29.0.37.0", {"start": v(121.22, 68.06) * mm, "end": v(121.22, -68.95) * mm});
            skLineSegment(sketch, "E29.3.37.0", {"start": v(120.72, 68.06) * mm, "end": v(120.72, -68.95) * mm});
            skLineSegment(sketch, "E29.6.37.0", {"start": v(120.72, 68.06) * mm, "end": v(121.22, 68.06) * mm});
            skLineSegment(sketch, "E29.9.37.0", {"start": v(120.72, -68.95) * mm, "end": v(121.22, -68.95) * mm});
            skLineSegment(sketch, "E29.0.38.0", {"start": v(129.22, 68.06) * mm, "end": v(129.22, -68.95) * mm});
            skLineSegment(sketch, "E29.3.38.0", {"start": v(128.72, 68.06) * mm, "end": v(128.72, -68.95) * mm});
            skLineSegment(sketch, "E29.6.38.0", {"start": v(128.72, 68.06) * mm, "end": v(129.22, 68.06) * mm});
            skLineSegment(sketch, "E29.9.38.0", {"start": v(128.72, -68.95) * mm, "end": v(129.22, -68.95) * mm});
            skLineSegment(sketch, "E29.0.39.0", {"start": v(137.22, 68.06) * mm, "end": v(137.22, -68.95) * mm});
            skLineSegment(sketch, "E29.3.39.0", {"start": v(136.72, 68.06) * mm, "end": v(136.72, -68.95) * mm});
            skLineSegment(sketch, "E29.6.39.0", {"start": v(136.72, 68.06) * mm, "end": v(137.22, 68.06) * mm});
            skLineSegment(sketch, "E29.9.39.0", {"start": v(136.72, -68.95) * mm, "end": v(137.22, -68.95) * mm});
            skLineSegment(sketch, "E29.0.40.0", {"start": v(145.22, 68.06) * mm, "end": v(145.22, -68.95) * mm});
            skLineSegment(sketch, "E29.3.40.0", {"start": v(144.72, 68.06) * mm, "end": v(144.72, -68.95) * mm});
            skLineSegment(sketch, "E29.6.40.0", {"start": v(144.72, 68.06) * mm, "end": v(145.22, 68.06) * mm});
            skLineSegment(sketch, "E29.9.40.0", {"start": v(144.72, -68.95) * mm, "end": v(145.22, -68.95) * mm});
            skLineSegment(sketch, "E29.0.41.0", {"start": v(153.22, 68.06) * mm, "end": v(153.22, -68.95) * mm});
            skLineSegment(sketch, "E29.3.41.0", {"start": v(152.72, 68.06) * mm, "end": v(152.72, -68.95) * mm});
            skLineSegment(sketch, "E29.6.41.0", {"start": v(152.72, 68.06) * mm, "end": v(153.22, 68.06) * mm});
            skLineSegment(sketch, "E29.9.41.0", {"start": v(152.72, -68.95) * mm, "end": v(153.22, -68.95) * mm});
            skLineSegment(sketch, "E29.0.42.0", {"start": v(161.22, 68.06) * mm, "end": v(161.22, -68.95) * mm});
            skLineSegment(sketch, "E29.3.42.0", {"start": v(160.72, 68.06) * mm, "end": v(160.72, -68.95) * mm});
            skLineSegment(sketch, "E29.6.42.0", {"start": v(160.72, 68.06) * mm, "end": v(161.22, 68.06) * mm});
            skLineSegment(sketch, "E29.9.42.0", {"start": v(160.72, -68.95) * mm, "end": v(161.22, -68.95) * mm});
            skLineSegment(sketch, "E29.0.43.0", {"start": v(169.22, 68.06) * mm, "end": v(169.22, -68.95) * mm});
            skLineSegment(sketch, "E29.3.43.0", {"start": v(168.72, 68.06) * mm, "end": v(168.72, -68.95) * mm});
            skLineSegment(sketch, "E29.6.43.0", {"start": v(168.72, 68.06) * mm, "end": v(169.22, 68.06) * mm});
            skLineSegment(sketch, "E29.9.43.0", {"start": v(168.72, -68.95) * mm, "end": v(169.22, -68.95) * mm});
            skSolve(sketch);
        }
        {
            var Q0;
            Q0 = qSketchRegion(id + "F11", true);
            extrude(context, id + "F12", {"entities" : qUnion([Q0]), "oppositeDirection" : true, "depth" : 1 * mm, "offsetDistance" : 25 * mm});
        }
        {
            var Q0;
            Q0=makeQuery(id+"F10.opExtrude","CAP_FACE",FACE,{"disambiguationData":[OSD([sQuery(id+"F8.wireOp",EDGE,"E9.bottom"),sQuery(id+"F8.wireOp",EDGE,"E9.top"),sQuery(id+"F8.wireOp",EDGE,"E9.left"),sQuery(id+"F8.wireOp",EDGE,"E9.right")])],"isStart":true});
            var sketch = newSketch(context, id + "F13", { "sketchPlane" : qUnion([Q0])});
            skCircle(sketch, "E30", {"center": v(0, 0) * mm, "radius": 50 * mm});
            skSolve(sketch);
        }
        {
            var Q0;
            Q0 = qSketchRegion(id + "F13", true);
            extrude(context, id + "F14", {"entities" : qUnion([Q0]), "depth" : 150 * mm, "offsetDistance" : 25 * mm});
        }
        {
            var Q0;
            Q0=makeQuery(id+"F14.opExtrude","CAP_FACE",FACE,{"disambiguationData":[OSD([sQuery(id+"F13.wireOp",EDGE,"E30")])],"isStart":false});
            var sketch = newSketch(context, id + "F15", { "sketchPlane" : qUnion([Q0])});
            skCircle(sketch, "E31", {"center": v(0, 0) * mm, "radius": 37.5 * mm});
            skSolve(sketch);
        }
        {
            var Q0;
            Q0=makeQuery(id+"F15.imprint","IMPRINT",FACE,{"disambiguationData":[TD([[makeQuery(id+"F15.imprint","IMPRINT",EDGE,{"derivedFrom":sQuery(id+"F15.wireOp",EDGE,"E31")}),1.0]])]});
            extrude(context, id + "F16", {"entities" : qUnion([Q0]), "operationType" : NewBodyOperationType.ADD, "depth" : 30 * mm, "offsetDistance" : 25 * mm});
        }
        {
            var Q0;
            Q0=makeQuery(id+"F14.opExtrude","CAP_EDGE",EDGE,{"disambiguationData":[OSD([sQuery(id+"F13.wireOp",EDGE,"E30")])],"isStart":false});
            var Q1;
            Q1=makeQuery(id+"F16.opExtrude","CAP_EDGE",EDGE,{"disambiguationData":[OSD([sQuery(id+"F15.wireOp",EDGE,"E31")])],"isStart":true});
            var Q2;
            Q2=makeQuery(id+"F14.opExtrude","CAP_EDGE",EDGE,{"disambiguationData":[OSD([sQuery(id+"F13.wireOp",EDGE,"E30")])],"isStart":true});
            var Q3;
            Q3=makeQuery(id+"F16.opExtrude","CAP_EDGE",EDGE,{"disambiguationData":[OSD([sQuery(id+"F15.wireOp",EDGE,"E31")])],"isStart":false});
            fillet(context, id + "F17", {"entities" : qUnion([Q0, Q1, Q2, Q3]), "radius" : 5 * mm, "tangentPropagation" : true, "allowEdgeOverflow" : false});
        }
        {
            var Q0;
            Q0=makeQuery(id+"F6.imprint","IMPRINT",FACE,{"disambiguationData":[TD([[makeQuery(id+"F6.imprint","IMPRINT",EDGE,{"derivedFrom":sQuery(id+"F6.wireOp",EDGE,"E2")}),-1.0]])]});
            var sketch = newSketch(context, id + "F18", { "sketchPlane" : qUnion([Q0])});
            skCircle(sketch, "E32", {"center": v(0, 0) * mm, "radius": 40 * mm});
            skSolve(sketch);
        }
        {
            var Q0;
            Q0 = qSketchRegion(id + "F18", true);
            extrude(context, id + "F19", {"entities" : qUnion([Q0]), "operationType" : NewBodyOperationType.ADD, "depth" : 20 * mm, "offsetDistance" : 25 * mm});
        }
        {
            var Q0;
            Q0=makeQuery(id+"F19.opExtrude","CAP_FACE",FACE,{"disambiguationData":[OSD([sQuery(id+"F18.wireOp",EDGE,"E32")])],"isStart":false});
            var sketch = newSketch(context, id + "F20", { "sketchPlane" : qUnion([Q0])});
            skCircle(sketch, "E33", {"center": v(0, 0) * mm, "radius": 18.75 * mm});
            skSolve(sketch);
        }
        {
            var Q0;
            Q0=makeQuery(id+"F20.imprint","IMPRINT",FACE,{"disambiguationData":[TD([[makeQuery(id+"F20.imprint","IMPRINT",EDGE,{"derivedFrom":sQuery(id+"F20.wireOp",EDGE,"E33")}),1.0]])]});
            extrude(context, id + "F21", {"entities" : qUnion([Q0]), "operationType" : NewBodyOperationType.ADD, "depth" : 25 * mm, "offsetDistance" : 25 * mm});
        }
        {
            var Q0;
            Q0=makeQuery(id+"F21.opExtrude","SWEPT_FACE",FACE,{"disambiguationData":[OSD([sQuery(id+"F20.wireOp",EDGE,"E33")])]});
            cPlane(context, id + "F22", {"entities" : qUnion([Q0]), "cplaneType" : CPlaneType.LINE_ANGLE, "offset" : 0 * mm, "angle" : 0 * degree, "width" : 150 * mm, "height" : 150 * mm});
        }
        {
            var Q0;
            Q0=qCreatedBy(id+"F22.planeOp",FACE);
            var sketch = newSketch(context, id + "F23", { "sketchPlane" : qUnion([Q0])});
            skArc(sketch, "E34", {"start": v(0, -120) * mm, "mid": v(45.38, -80) * mm, "end": v(0, -40) * mm});
            skLineSegment(sketch, "E35", {"start": v(0, -40) * mm, "end": v(0, -120) * mm});
            skSolve(sketch);
        }
        {
            var Q0;
            Q0=makeQuery(id+"F23.imprint","IMPRINT",FACE,{"disambiguationData":[TD([[makeQuery(id+"F23.imprint","IMPRINT",EDGE,{"derivedFrom":sQuery(id+"F23.wireOp",EDGE,"E34")}),1.0]])]});
            var Q1;
            Q1=sQuery(id+"F23.wireOp",EDGE,"E35");
            revolve(context, id + "F24", {"operationType" : NewBodyOperationType.ADD, "entities" : qUnion([Q0]), "axis" : qUnion([Q1]), "revolveType" : RevolveType.FULL});
        }
        {
            var Q0;
            Q0=makeQuery(id+"F4.opLoft","CAP_FACE",FACE,{"disambiguationData":[OSD([makeQuery(id+"F3.imprint","IMPRINT",FACE,{"disambiguationData":[TD([[makeQuery(id+"F3.imprint","IMPRINT",EDGE,{"derivedFrom":sQuery(id+"F3.wireOp",EDGE,"E1.bottom")}),1.0]])]})])],"isStart":true});
            var sketch = newSketch(context, id + "F25", { "sketchPlane" : qUnion([Q0])});
            skLineSegment(sketch, "E36.bottom", {"start": v(-275, 167.5) * mm, "end": v(275, 167.5) * mm});
            skLineSegment(sketch, "E36.top", {"start": v(-275, -167.5) * mm, "end": v(275, -167.5) * mm});
            skLineSegment(sketch, "E36.left", {"start": v(-275, 167.5) * mm, "end": v(-275, -167.5) * mm});
            skLineSegment(sketch, "E36.right", {"start": v(275, 167.5) * mm, "end": v(275, -167.5) * mm});
            skSolve(sketch);
        }
        {
            var Q0;
            Q0=makeQuery(id+"F25.imprint","IMPRINT",FACE,{"disambiguationData":[TD([[makeQuery(id+"F25.imprint","IMPRINT",EDGE,{"derivedFrom":sQuery(id+"F25.wireOp",EDGE,"E36.bottom")}),1.0]])]});
            var Q1;
            {var subQ0=sQuery(id+"F3.wireOp",EDGE,"E1.right");var subQ1=sQuery(id+"F3.wireOp",EDGE,"E1.left");var subQ2=sQuery(id+"F3.wireOp",EDGE,"E1.bottom");Q1=makeQuery(id+"F25.imprint","IMPRINT",FACE,{"disambiguationData":[TD([[makeQuery(id+"F25.imprint","IMPRINT",EDGE,{"derivedFrom":makeQuery(id+"F5.opShell","OFFSET_EDGE",EDGE,{"disambiguationData":[OSD([subQ2,subQ1,subQ0])]})}),1.0]])]});}
            extrude(context, id + "F26", {"entities" : qUnion([Q0, Q1]), "operationType" : NewBodyOperationType.ADD, "depth" : 20 * mm, "offsetDistance" : 25 * mm});
        }
        {
            var Q0;
            Q0=makeQuery(id+"F4.opLoft","SWEPT_FACE",FACE,{"disambiguationData":[OSD([sQuery(id+"F2.wireOp",EDGE,"E0.bottom"),sQuery(id+"F2.wireOp",EDGE,"E0.top"),sQuery(id+"F2.wireOp",EDGE,"E0.left"),sQuery(id+"F3.wireOp",EDGE,"E1.bottom"),sQuery(id+"F3.wireOp",EDGE,"E1.top"),sQuery(id+"F3.wireOp",EDGE,"E1.left")])]});
            var sketch = newSketch(context, id + "F27", { "sketchPlane" : qUnion([Q0])});
            skCircle(sketch, "E37", {"center": v(0, -38.1) * mm, "radius": 1.99 * mm});
            skCircle(sketch, "E38", {"center": v(0, 116.9) * mm, "radius": 2.5 * mm});
            skSolve(sketch);
        }
        {
            var Q0;
            Q0=makeQuery(id+"F27.imprint","IMPRINT",FACE,{"disambiguationData":[TD([[makeQuery(id+"F27.imprint","IMPRINT",EDGE,{"derivedFrom":sQuery(id+"F27.wireOp",EDGE,"E37")}),1.0]])]});
            extrude(context, id + "F28", {"entities" : qUnion([Q0]), "operationType" : NewBodyOperationType.ADD, "endBound" : BoundingType.SYMMETRIC, "depth" : 150 * mm, "offsetDistance" : 25 * mm});
        }
        {
            var Q0;
            Q0=makeQuery(id+"F26.opExtrude","CAP_FACE",FACE,{"disambiguationData":[OSD([sQuery(id+"F25.wireOp",EDGE,"E36.bottom"),sQuery(id+"F25.wireOp",EDGE,"E36.top"),sQuery(id+"F25.wireOp",EDGE,"E36.left"),sQuery(id+"F25.wireOp",EDGE,"E36.right")])],"isStart":false});
            var sketch = newSketch(context, id + "F29", { "sketchPlane" : qUnion([Q0])});
            skCircle(sketch, "E39", {"center": v(0, 0) * mm, "radius": 2.5 * mm});
            skCircle(sketch, "E40", {"center": v(125, 0) * mm, "radius": 2.5 * mm});
            skSolve(sketch);
        }
        {
            var Q0;
            Q0=makeQuery(id+"F29.imprint","IMPRINT",FACE,{"disambiguationData":[TD([[makeQuery(id+"F29.imprint","IMPRINT",EDGE,{"derivedFrom":sQuery(id+"F29.wireOp",EDGE,"E40")}),1.0]])]});
            extrude(context, id + "F30", {"entities" : qUnion([Q0]), "endBound" : BoundingType.SYMMETRIC, "depth" : 200 * mm, "offsetDistance" : 25 * mm});
        }
    });
